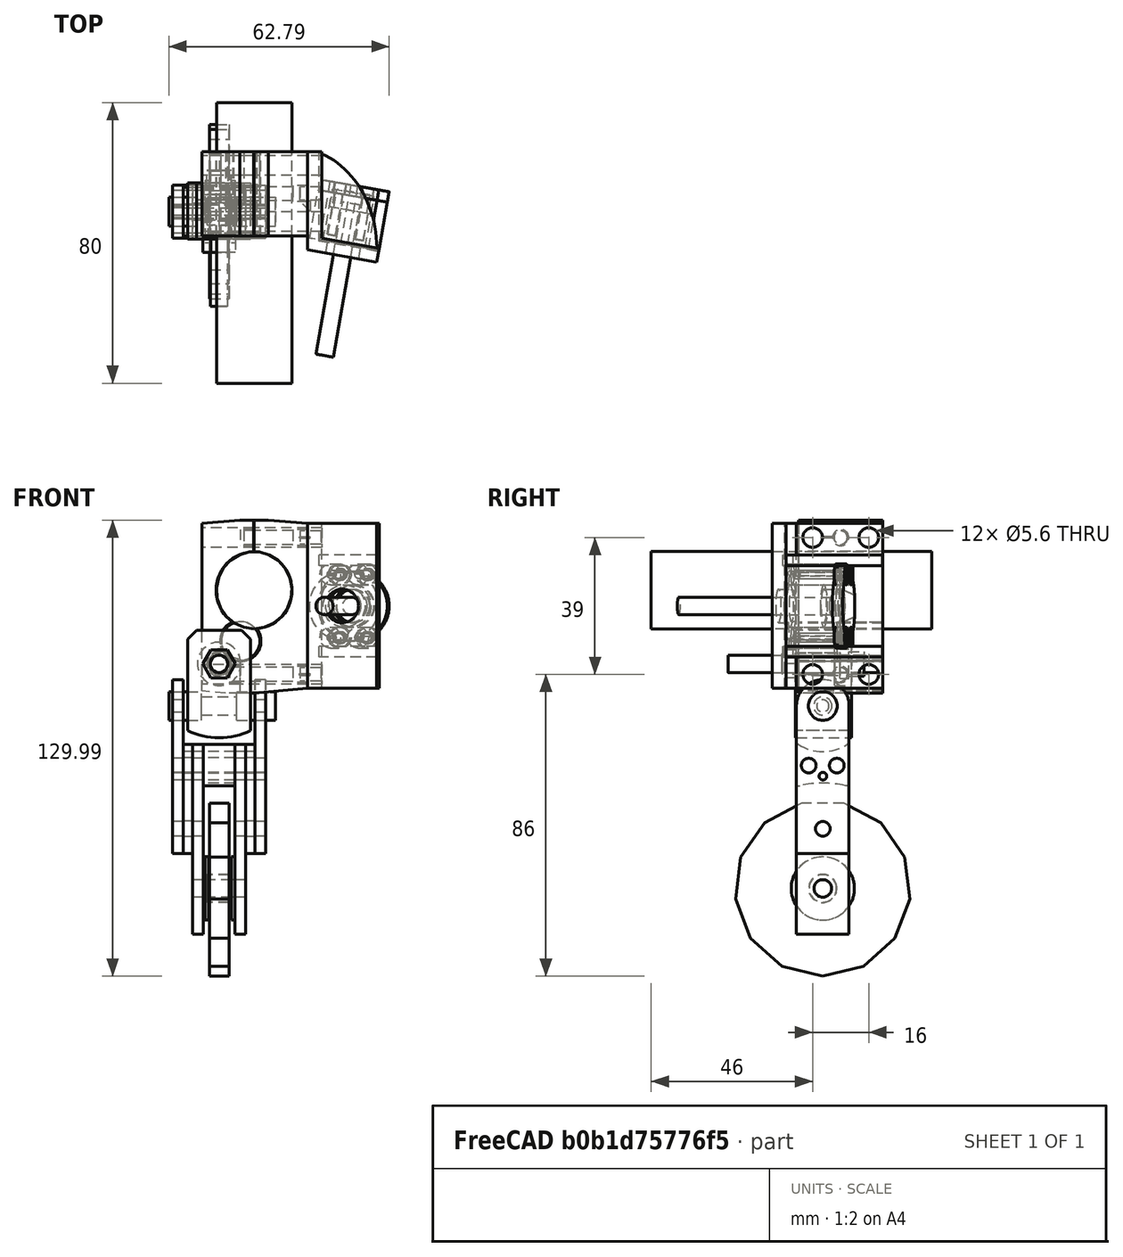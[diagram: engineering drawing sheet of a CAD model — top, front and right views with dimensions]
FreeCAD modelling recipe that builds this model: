
FCSTD DOCUMENT  (FreeCAD 0.18R4 (GitTag))
Label: ~ketten_spanner_118
License: All rights reserved
LicenseURL: http://en.wikipedia.org/wiki/All_rights_reserved
objects: Part::Cylinder×56, Part::Cut×43, Sketcher::SketchObject×37, PartDesign::Body×37, App::DocumentObjectGroup×35, PartDesign::Pad×29, App::Part×13, PartDesign::Revolution×5, Mesh::Feature×3
note: 241 computed .brp shape members not serialized (recipe doc carries the construction recipe); baked Part::Feature solids carry a one-line shape summary decoded from their .brp

FEATURE [Sketcher::SketchObject] Sketch001
  MapMode = 5
  Placement = pos=(0,0,0) rot=(1,0,0;1.5708rad)
  Support = -> [XZ_Plane002]
  sketch-geometry (6):
    g0: Ellipse CenterX=10 CenterY=21 CenterZ=0 NormalX=0 NormalY=0 NormalZ=1 MajorRadius=11 MinorRadius=10.75 AngleXU=-1.5708
    g1: LineSegment [constr] StartX=10 StartY=10 StartZ=0 EndX=10 EndY=32 EndZ=0
    g2: LineSegment [constr] StartX=20.75 StartY=21 StartZ=0 EndX=-0.75 EndY=21 EndZ=0
    g3: GeomPoint X=10 Y=18.6682 Z=0
    g4: GeomPoint X=10 Y=23.3318 Z=0
    g5: LineSegment [constr] StartX=-7.94652 StartY=18.6682 StartZ=0 EndX=23.4716 EndY=18.6682 EndZ=0
  constraints (8):
    c: InternalAlignment(g1-g4 -> g0) x4
    c: Vertical(g1)
    c: DistanceY(g1,g1) = 22
    c: DistanceX(g2,g2) = 21.5
    c: DistanceX(g-1,g1) = 10
    c: DistanceY(g-1,g1) = 10
    c: Horizontal(g5)
    c: PointOnObject(g3,g5)
FEATURE [PartDesign::Pad] Pad
  Length = 80
  Length2 = 100
  Placement = pos=(0,0,0) rot=(1,0,0;1.5708rad)
  Profile = -> Sketch001
  Type = 0
FEATURE [PartDesign::Body] Body001  label="schwinge_P"
  Group = -> [Sketch001,Pad]
  Origin = -> Origin002
  Placement = pos=(0,14,0) rot=(0,0,1;0rad)
  Tip = -> Pad
FEATURE [Sketcher::SketchObject] Sketch002
  MapMode = 5
  Placement = pos=(0,0,0) rot=(1,0,0;1.5708rad)
  Support = -> [XZ_Plane004]
  sketch-geometry (14):
    g0: ArcOfCircle CenterX=6.11771 CenterY=6.51111 CenterZ=0 NormalX=0 NormalY=0 NormalZ=1 AngleXU=0 Radius=5.5 StartAngle=4.88029 EndAngle=10.3041
    g1: LineSegment [constr] StartX=-14.7828 StartY=10 StartZ=0 EndX=10 EndY=10 EndZ=0
    g2: LineSegment [constr] StartX=7.54122 StartY=11.8237 StartZ=0 EndX=-1.04375 EndY=-20.2158 EndZ=0
    g3: LineSegment StartX=2.6104 StartY=2.27451 StartZ=0 EndX=7.03683 EndY=1.08845 EndZ=0
    g4: LineSegment [constr] StartX=2.6104 StartY=2.27451 StartZ=0 EndX=5.328 EndY=12.4167 EndZ=0
    g5: LineSegment [constr] StartX=5.328 StartY=12.4167 StartZ=0 EndX=7.54122 EndY=11.8237 EndZ=0
    g6: LineSegment [constr] StartX=10 StartY=34.9897 StartZ=0 EndX=10 EndY=-5.77115 EndZ=0
    g7: LineSegment [constr] StartX=10 StartY=21 StartZ=0 EndX=-1.04375 EndY=-20.2158 EndZ=0
    g8: LineSegment [constr] StartX=10 StartY=10 StartZ=0 EndX=10 EndY=32 EndZ=0
    g9: LineSegment [constr] StartX=-6.34284 StartY=21 StartZ=0 EndX=23.447 EndY=21 EndZ=0
    g10: LineSegment [constr] StartX=8.31393 StartY=14.7075 StartZ=0 EndX=12.847 EndY=31.6252 EndZ=0
    g11: Circle [constr] CenterX=10 CenterY=21 CenterZ=0 NormalX=0 NormalY=0 NormalZ=1 AngleXU=0 Radius=11
    g12: LineSegment [constr] StartX=4.48461 StartY=9.26913 StartZ=0 EndX=10.6338 EndY=32.2182 EndZ=0
    g13: LineSegment [constr] StartX=10.6338 StartY=32.2182 StartZ=0 EndX=12.847 EndY=31.6252 EndZ=0
  constraints (38):
    c: Horizontal(g1)
    c: DistanceY(g-1,g1) = 10
    c: PointOnObject(g0,g2)
    c: Coincident(g3,g0)
    c: Coincident(g3,g0)
    c: Radius(g0) = 5.5
    c: PointOnObject(g2,g0)
    c: Perpendicular(g2,g3)
    c: Coincident(g4,g0)
    c: Parallel(g4,g2)
    c: Coincident(g5,g2)
    c: Coincident(g5,g4)
    c: Perpendicular(g5,g4)
    c: Vertical(g6)
    c: DistanceX(g-1,g6) = 10
    c: PointOnObject(g7,g6)
    c: Angle(g6,g7) = -0.261799
    c: PointOnObject(g2,g7)
    c: Coincident(g2,g7)
    c: Vertical(g8)
    c: PointOnObject(g8,g1)
    c: DistanceY(g8,g8) = 22
    c: PointOnObject(g8,g6)
    c: Horizontal(g9)
    c: Symmetric(g1,g8,g9)
    c: PointOnObject(g7,g9)
    c: PointOnObject(g10,g7)
    c: Parallel(g10,g2)
    c: Coincident(g11,g7)
    c: Radius(g11) = 11
    c: PointOnObject(g10,g11)
    c: Distance(g10,g0) = 26
    c: PointOnObject(g12,g4)
    c: Parallel(g12,g4)
    c: Coincident(g13,g12)
    c: Coincident(g13,g10)
    c: Perpendicular(g12,g13)
    c: Distance(g12,g0) = 31
FEATURE [PartDesign::Pad] Pad001
  Length = 13
  Length2 = 100
  Placement = pos=(0,0,0) rot=(1,0,0;1.5708rad)
  Profile = -> Sketch002
  Type = 0
FEATURE [PartDesign::Body] Body  label="Bremsspanner_P"
  Group = -> [Sketch002,Pad001]
  Origin = -> Origin003
  Tip = -> Pad001
FEATURE [PartDesign::Body] Body002  label="klemme_P"
  Origin = -> Origin005
FEATURE [PartDesign::Body] Body003  label="platte_P"
  Origin = -> Origin006
FEATURE [Sketcher::SketchObject] Sketch
  MapMode = 5
  Placement = pos=(0,0,0) rot=(1,0,0;1.5708rad)
  sketch-geometry (22):
    g0: LineSegment [constr] StartX=9.89353 StartY=-3.73516 StartZ=0 EndX=9.89353 EndY=38.9018 EndZ=0
    g1: ArcOfCircle CenterX=6.01 CenterY=6.5 CenterZ=0 NormalX=0 NormalY=0 NormalZ=1 AngleXU=0 Radius=5.8 StartAngle=1.95124 EndAngle=4.69231
    g2: LineSegment [constr] StartX=5.89353 StartY=0.701169 StartZ=0 EndX=6.01 EndY=6.5 EndZ=0
    g3: LineSegment [constr] StartX=6.01 StartY=6.5 StartZ=0 EndX=3.85628 EndY=11.8853 EndZ=0
    g4: LineSegment [constr] StartX=9.89353 StartY=20.9935 StartZ=0 EndX=-1.15445 EndY=-20.2381 EndZ=0
    g5: LineSegment [constr] StartX=9.89353 StartY=20.9935 StartZ=0 EndX=9.89353 EndY=-21.8961 EndZ=0
    g6: ArcOfEllipse CenterX=9.89353 CenterY=20.9935 CenterZ=0 NormalX=0 NormalY=0 NormalZ=1 MajorRadius=11 MinorRadius=10.7674 AngleXU=1.5708 StartAngle=0 EndAngle=2.54637
    g7: LineSegment [constr] StartX=9.89353 StartY=31.9935 StartZ=0 EndX=9.89353 EndY=9.99354 EndZ=0
    g8: GeomPoint X=9.89353 Y=23.2435 Z=0
    g9: GeomPoint X=9.89353 Y=18.7435 Z=0
    g10: LineSegment [constr] StartX=8.83076 StartY=17.0272 StartZ=0 EndX=12.6435 EndY=31.2567 EndZ=0
    g11: LineSegment [constr] StartX=9.89353 StartY=31.9935 StartZ=0 EndX=12.6435 EndY=31.2567 EndZ=0
    g12: LineSegment StartX=5.89353 StartY=0.701169 StartZ=0 EndX=5.89353 EndY=-8.29883 EndZ=0
    g13: LineSegment StartX=5.89353 StartY=-8.29883 StartZ=0 EndX=1.89353 EndY=-8.29883 EndZ=0
    g14: LineSegment StartX=1.89353 StartY=-8.29883 StartZ=0 EndX=-4.8739 EndY=-7.70676 EndZ=0
    g15: LineSegment StartX=-4.8739 StartY=-7.70676 StartZ=0 EndX=-4.8739 EndY=40.0515 EndZ=0
    g16: LineSegment StartX=-4.8739 StartY=40.0515 StartZ=0 EndX=5.89353 EndY=40.9935 EndZ=0
    g17: LineSegment StartX=5.89353 StartY=40.9935 StartZ=0 EndX=9.89353 EndY=40.9935 EndZ=0
    g18: LineSegment StartX=9.89353 StartY=40.9935 StartZ=0 EndX=9.89353 EndY=31.9935 EndZ=0
    g19: LineSegment [constr] StartX=1.89353 StartY=-8.29883 StartZ=0 EndX=-7.766 EndY=-8.29883 EndZ=0
    g20: LineSegment [constr] StartX=5.89353 StartY=40.9935 StartZ=0 EndX=-7.21475 EndY=40.9935 EndZ=0
    g21: LineSegment [constr] StartX=9.89353 StartY=20.9935 StartZ=0 EndX=-0.873896 EndY=20.9935 EndZ=0
  constraints (56):
    c: Vertical(g0)
    c: Radius(g1) = 5.8
    c: Coincident(g2,g1)
    c: Coincident(g2,g1)
    c: Coincident(g3,g1)
    c: Vertical(g5)
    c: Angle(g5,g4) = -0.261799
    c: PointOnObject(g1,g4)
    c: InternalAlignment(g7,g6)
    c: InternalAlignment(g8,g6)
    c: InternalAlignment(g9,g6)
    c: Vertical(g7)
    c: Coincident(g4,g5)
    c: Coincident(g4,g6)
    c: PointOnObject(g10,g4)
    c: Coincident(g11,g7)
    c: Coincident(g11,g10)
    c: Parallel(g10,g4)
    c: Perpendicular(g10,g11)
    c: Coincident(g12,g13)
    c: Coincident(g13,g14)
    c: Coincident(g14,g15)
    c: Vertical(g15)
    c: Coincident(g15,g16)
    c: Coincident(g16,g17)
    c: Coincident(g17,g18)
    c: Vertical(g18)
    c: Coincident(g12,g1)
    c: Coincident(g6,g18)
    c: Vertical(g12)
    c: Horizontal(g13)
    c: Coincident(g19,g13)
    c: Horizontal(g19)
    c: Angle(g14,g19) = 0.0872665
    c: Horizontal(g17)
    c: DistanceY(g6,g17) = 9
    c: Coincident(g20,g16)
    c: Horizontal(g20)
    c: Angle(g20,g16) = 0.0872665
    c: DistanceX(g13,g12) = 4
    c: DistanceX(g16,g17) = 4
    c: DistanceX(g-1,g1) = 6.01
    c: PointOnObject(g17,g0)
    c: DistanceY(g-1,g1) = 6.5
    c: Coincident(g3,g1)
    c: Coincident(g1,g6)
    c: PointOnObject(g0,g5)
    c: DistanceY(g7,g6) = 22
    c: DistanceY(g12,g1) = 9
    c: Distance(g1,g10) = 25.63
    c: DistanceX(g12,g5) = 4
    c: Coincident(g21,g6)
    c: Horizontal(g21)
    c: PointOnObject(g21,g6)
    c: DistanceX(g14,g21) = 4
    c: DistanceY(g9,g8) = 4.5
FEATURE [PartDesign::Pad] Pad002
  Length = 24
  Length2 = 100
  Placement = pos=(0,0,0) rot=(1,0,0;1.5708rad)
  Profile = -> Sketch
  Type = 0
FEATURE [Sketcher::SketchObject] Sketch003
  MapMode = 5
  Placement = pos=(0,0,0) rot=(1,0,0;1.5708rad)
  sketch-geometry (25):
    g0: LineSegment [constr] StartX=10 StartY=-2.49556 StartZ=0 EndX=10 EndY=51.298 EndZ=0
    g1: ArcOfCircle CenterX=6.11647 CenterY=6.5 CenterZ=0 NormalX=0 NormalY=0 NormalZ=1 AngleXU=0 Radius=5.8 StartAngle=4.69231 EndAngle=6.93504
    g2: LineSegment [constr] StartX=10.7272 StartY=10.0187 StartZ=0 EndX=6.11647 EndY=6.5 EndZ=0
    g3: LineSegment [constr] StartX=6.11647 StartY=6.5 StartZ=0 EndX=6 EndY=0.701169 EndZ=0
    g4: LineSegment [constr] StartX=10 StartY=20.9935 StartZ=0 EndX=-1.05913 EndY=-20.2797 EndZ=0
    g5: LineSegment [constr] StartX=10 StartY=20.9935 StartZ=0 EndX=10 EndY=-21.8961 EndZ=0
    g6: ArcOfEllipse CenterX=10 CenterY=20.9935 CenterZ=0 NormalX=0 NormalY=0 NormalZ=1 MajorRadius=11 MinorRadius=10.7674 AngleXU=1.5708 StartAngle=3.20918 EndAngle=6.28319
    g7: LineSegment [constr] StartX=10 StartY=31.9935 StartZ=0 EndX=10 EndY=9.99354 EndZ=0
    g8: GeomPoint X=10 Y=23.2435 Z=0
    g9: GeomPoint X=10 Y=18.7435 Z=0
    g10: LineSegment [constr] StartX=8.44517 StartY=15.1908 StartZ=0 EndX=12.75 EndY=31.2567 EndZ=0
    g11: LineSegment [constr] StartX=10 StartY=31.9935 StartZ=0 EndX=12.75 EndY=31.2567 EndZ=0
    g12: LineSegment [constr] StartX=2.90768 StartY=-8 StartZ=0 EndX=-7.766 EndY=-8 EndZ=0
    g13: LineSegment [constr] StartX=6 StartY=40.954 StartZ=0 EndX=-7.21475 EndY=40.954 EndZ=0
    g14: LineSegment StartX=10 StartY=31.9935 StartZ=0 EndX=10 EndY=40.9935 EndZ=0
    g15: LineSegment StartX=10 StartY=40.9935 StartZ=0 EndX=14 EndY=40.9935 EndZ=0
    g16: LineSegment StartX=14 StartY=40.9935 StartZ=0 EndX=25.2674 EndY=40.0078 EndZ=0
    g17: LineSegment StartX=25.2674 StartY=40.0078 StartZ=0 EndX=25.2674 EndY=-6.9631 EndZ=0
    g18: LineSegment StartX=25.2674 StartY=-6.9631 StartZ=0 EndX=10 EndY=-8.29883 EndZ=0
    g19: LineSegment StartX=10 StartY=-8.29883 StartZ=0 EndX=6 EndY=-8.29883 EndZ=0
    g20: LineSegment StartX=6 StartY=-8.29883 StartZ=0 EndX=6 EndY=0.701169 EndZ=0
    g21: LineSegment [constr] StartX=10 StartY=-8.29883 StartZ=0 EndX=29.3759 EndY=-8.29883 EndZ=0
    g22: LineSegment [constr] StartX=14 StartY=40.9935 StartZ=0 EndX=28.0792 EndY=40.9935 EndZ=0
    g23: LineSegment [constr] StartX=6 StartY=0.701169 StartZ=0 EndX=16.0779 EndY=0.701169 EndZ=0
    g24: LineSegment [constr] StartX=10 StartY=20.9935 StartZ=0 EndX=20.7674 EndY=20.9935 EndZ=0
  constraints (60):
    c: Vertical(g0)
    c: Radius(g1) = 5.8
    c: Coincident(g2,g1)
    c: Coincident(g2,g1)
    c: Coincident(g3,g1)
    c: Coincident(g3,g1)
    c: Vertical(g5)
    c: Angle(g5,g4) = -0.261799
    c: PointOnObject(g1,g4)
    c: InternalAlignment(g7,g6)
    c: InternalAlignment(g8,g6)
    c: InternalAlignment(g9,g6)
    c: Vertical(g7)
    c: DistanceX(g-1,g6) = 10
    c: Coincident(g4,g5)
    c: Coincident(g4,g6)
    c: PointOnObject(g10,g4)
    c: PointOnObject(g0,g7)
    c: Coincident(g11,g7)
    c: Coincident(g11,g10)
    c: Parallel(g10,g4)
    c: Perpendicular(g10,g11)
    c: Distance(g10,g1) = 25.63
    c: Horizontal(g12)
    c: Horizontal(g13)
    c: Coincident(g6,g1)
    c: Vertical(g14)
    c: Coincident(g14,g15)
    c: Horizontal(g15)
    c: Coincident(g15,g16)
    c: Coincident(g16,g17)
    c: Vertical(g17)
    c: Coincident(g18,g19)
    c: Horizontal(g19)
    c: Coincident(g19,g20)
    c: Vertical(g20)
    c: Coincident(g20,g1)
    c: Coincident(g14,g6)
    c: Horizontal(g21)
    c: DistanceX(g14,g15) = 4
    c: Coincident(g22,g15)
    c: Horizontal(g22)
    c: Angle(g16,g22) = 0.0872665
    c: DistanceY(g7,g7) = 22
    c: Coincident(g23,g1)
    c: Horizontal(g23)
    c: DistanceY(g6,g14) = 9
    c: DistanceY(g-1,g1) = 6.5
    c: PointOnObject(g14,g0)
    c: DistanceX(g19,g5) = 4
    c: Coincident(g24,g6)
    c: Horizontal(g24)
    c: PointOnObject(g24,g6)
    c: DistanceX(g24,g17) = 4.5
    c: Coincident(g18,g17)
    c: PointOnObject(g18,g5)
    c: Coincident(g21,g18)
    c: Angle(g21,g18) = 0.0872665
    c: DistanceY(g21,g23) = 9
    c: DistanceY(g9,g8) = 4.5
FEATURE [PartDesign::Pad] Pad003
  Length = 24
  Length2 = 100
  Placement = pos=(0,0,0) rot=(1,0,0;1.5708rad)
  Profile = -> Sketch003
  Type = 0
FEATURE [Part::Cylinder] Cylinder  label="O1"
  Angle = 360
  AttacherType = Attacher::AttachEngine3D
  Height = 60
  Placement = pos=(41,-20,36) rot=(0,-1,0;1.5708rad)
  Radius = 2.8
FEATURE [Part::Cylinder] Cylinder001  label="O2"
  Angle = 360
  AttacherType = Attacher::AttachEngine3D
  Height = 60
  Placement = pos=(41,-4,36) rot=(0,-1,0;1.5708rad)
  Radius = 2.8
FEATURE [Part::Cylinder] Cylinder002  label="U001"
  Angle = 360
  AttacherType = Attacher::AttachEngine3D
  Height = 60
  Placement = pos=(41,-4,-3) rot=(0,-1,0;1.5708rad)
  Radius = 2.8
FEATURE [Part::Cylinder] Cylinder003  label="U002"
  Angle = 360
  AttacherType = Attacher::AttachEngine3D
  Height = 60
  Placement = pos=(41,-20,-3) rot=(0,-1,0;1.5708rad)
  Radius = 2.8
FEATURE [Part::Cylinder] Cylinder004  label="O003"
  Angle = 360
  AttacherType = Attacher::AttachEngine3D
  Height = 60
  Placement = pos=(41,-4,36) rot=(0,-1,0;1.5708rad)
  Radius = 2.8
FEATURE [Part::Cylinder] Cylinder005  label="U003"
  Angle = 360
  AttacherType = Attacher::AttachEngine3D
  Height = 60
  Placement = pos=(41,-20,-3) rot=(0,-1,0;1.5708rad)
  Radius = 2.8
FEATURE [Part::Cylinder] Cylinder006  label="U004"
  Angle = 360
  AttacherType = Attacher::AttachEngine3D
  Height = 60
  Placement = pos=(41,-4,-3) rot=(0,-1,0;1.5708rad)
  Radius = 2.8
FEATURE [Part::Cylinder] Cylinder007  label="O004"
  Angle = 360
  AttacherType = Attacher::AttachEngine3D
  Height = 60
  Placement = pos=(41,-20,36) rot=(0,-1,0;1.5708rad)
  Radius = 2.8
FEATURE [App::Part] Part002  label="Bremsspanner"
  Group = -> [Body]
  Origin = -> Origin007
  Placement = pos=(0,-5.5,0) rot=(0,0,1;0rad)
FEATURE [App::Part] Part005  label="Holm"
  Group = -> [Body001]
  Origin = -> Origin010
  Placement = pos=(0,2,0) rot=(0,0,1;0rad)
FEATURE [App::Part] Part  label="Basis"
  Group = -> [Part002,Part005]
  Origin = -> Origin
FEATURE [Part::Cylinder] Cylinder010  label="PassI_Pl-Kl0"
  Angle = 360
  AttacherType = Attacher::AttachEngine3D
  Height = 35
  Placement = pos=(41,-12,36) rot=(0,-1,0;1.5708rad)
  Radius = 2.3
FEATURE [Part::Cylinder] Cylinder011  label="PassI_Pl-Kl1"
  Angle = 360
  AttacherType = Attacher::AttachEngine3D
  Height = 39
  Placement = pos=(41,-12,-3) rot=(0,-1,0;1.5708rad)
  Radius = 2.3
FEATURE [Part::Cylinder] Cylinder012  label="PassO_Pl-Kl0"
  Angle = 360
  AttacherType = Attacher::AttachEngine3D
  Height = 14
  Placement = pos=(21,-12,36) rot=(0,-1,0;1.5708rad)
  Radius = 2
FEATURE [Part::Cylinder] Cylinder013  label="PassO_Pl-Kl1"
  Angle = 360
  AttacherType = Attacher::AttachEngine3D
  Height = 18
  Placement = pos=(21,-12,-3) rot=(0,-1,0;1.5708rad)
  Radius = 2
FEATURE [Part::Cylinder] Cylinder014  label="PassI_Kl-Wi0"
  Angle = 360
  AttacherType = Attacher::AttachEngine3D
  Height = 20
  Placement = pos=(41,-12,-3) rot=(0,-1,0;1.5708rad)
  Radius = 2.3
FEATURE [Part::Cylinder] Cylinder015  label="PassI_Kl-Wi1"
  Angle = 360
  AttacherType = Attacher::AttachEngine3D
  Height = 20
  Placement = pos=(41,-12,36) rot=(0,-1,0;1.5708rad)
  Radius = 2.3
FEATURE [Sketcher::SketchObject] Sketch005
  MapMode = 5
  Placement = pos=(0,0,0) rot=(1,0,0;1.5708rad)
  Support = -> [XZ_Plane016]
  sketch-geometry (12):
    g0: ArcOfEllipse CenterX=6.11474 CenterY=6.5 CenterZ=0 NormalX=0 NormalY=0 NormalZ=1 MajorRadius=5.5 MinorRadius=5.49977 AngleXU=1.309 StartAngle=0.640981 EndAngle=5.62359
    g1: LineSegment [constr] StartX=7.53824 StartY=11.8126 StartZ=0 EndX=4.69123 EndY=1.18741 EndZ=0
    g2: GeomPoint X=6.12768 Y=6.5483 Z=0
    g3: GeomPoint X=6.1018 Y=6.4517 Z=0
    g4: LineSegment [constr] StartX=10 StartY=27.7324 StartZ=0 EndX=10 EndY=-9.55565 EndZ=0
    g5: LineSegment [constr] StartX=10 StartY=21 StartZ=0 EndX=2.09145 EndY=-8.5151 EndZ=0
    g6: ArcOfEllipse CenterX=6.11474 CenterY=6.5 CenterZ=0 NormalX=0 NormalY=0 NormalZ=1 MajorRadius=5.8 MinorRadius=5.79978 AngleXU=-1.8326 StartAngle=3.79757 EndAngle=8.76184
    g7: LineSegment [constr] StartX=4.61359 StartY=0.89763 StartZ=0 EndX=7.61589 EndY=12.1024 EndZ=0
    g8: GeomPoint X=6.1018 Y=6.4517 Z=0
    g9: GeomPoint X=6.12768 Y=6.5483 Z=0
    g10: LineSegment StartX=10.4951 StartY=9.82594 StartZ=0 EndX=10.7457 EndY=9.99187 EndZ=0
    g11: LineSegment StartX=3.88738 StartY=11.8552 StartZ=0 EndX=4.07899 EndY=11.6093 EndZ=0
  constraints (24):
    c: InternalAlignment(g1,g0)
    c: InternalAlignment(g2,g0)
    c: InternalAlignment(g3,g0)
    c: Vertical(g4)
    c: DistanceX(g-1,g4) = 10
    c: PointOnObject(g5,g4)
    c: Angle(g5,g4) = 0.261799
    c: DistanceY(g-1,g5) = 21
    c: PointOnObject(g0,g5)
    c: PointOnObject(g1,g5)
    c: DistanceY(g-1,g0) = 6.5
    c: Distance(g1,g1) = 11
    c: Distance(g2,g3) = 0.1
    c: InternalAlignment(g7,g6)
    c: InternalAlignment(g8,g6)
    c: InternalAlignment(g9,g6)
    c: Distance(g9,g8) = 0.1
    c: PointOnObject(g7,g1)
    c: Distance(g7,g7) = 11.6
    c: Coincident(g6,g0)
    c: Coincident(g0,g11)
    c: Coincident(g11,g6)
    c: Coincident(g10,g0)
    c: Coincident(g10,g6)
FEATURE [PartDesign::Pad] Pad005
  Length = 24
  Length2 = 100
  Placement = pos=(0,0,0) rot=(1,0,0;1.5708rad)
  Profile = -> Sketch005
  Type = 0
FEATURE [PartDesign::Body] Body005  label="Pressung"
  Group = -> [Sketch005,Pad005]
  Origin = -> Origin015
  Tip = -> Pad005
FEATURE [App::Part] Part008  label="Einlage"
  Group = -> [Body005]
  Origin = -> Origin014
FEATURE [Part::Cut] Cut
  Base = -> Pad002
  Tool = -> Cylinder
FEATURE [Part::Cut] Cut010
  Base = -> Cut
  Tool = -> Cylinder002
FEATURE [Part::Cut] Cut011
  Base = -> Cut010
  Tool = -> Cylinder003
FEATURE [Part::Cut] Cut012
  Base = -> Cut011
  Tool = -> Cylinder001
FEATURE [Part::Cut] Cut013
  Base = -> Cut012
  Tool = -> Cylinder010
FEATURE [Part::Cut] Cut014
  Base = -> Cut013
  Tool = -> Cylinder011
FEATURE [App::Part] Part003  label="platte"
  Group = -> [Body003,Cylinder001,Cylinder003,Cylinder002,Cylinder,Sketch,Pad002,Cylinder010,Cylinder011,Cut,Cut010,Cut011,Cut012,Cut013,Cut014]
  Origin = -> Origin008
FEATURE [Part::Cut] Cut015
  Base = -> Pad003
  Tool = -> Cylinder007
FEATURE [Part::Cut] Cut016
  Base = -> Cut015
  Tool = -> Cylinder006
FEATURE [Part::Cut] Cut017
  Base = -> Cut016
  Tool = -> Cylinder005
FEATURE [Part::Cut] Cut018
  Base = -> Cut017
  Tool = -> Cylinder004
FEATURE [Part::Cut] Cut019
  Base = -> Cut018
  Tool = -> Cylinder015
FEATURE [Part::Cut] Cut020
  Base = -> Cut019
  Tool = -> Cylinder014
FEATURE [App::Part] Part004  label="klemme"
  Group = -> [Body002,Cylinder004,Cylinder005,Cylinder006,Cylinder007,Sketch003,Pad003,Cylinder012,Cylinder013,Cylinder014,Cylinder015,Cut015,Cut016,Cut017,Cut018,Cut019,Cut020]
  Origin = -> Origin009
FEATURE [App::DocumentObjectGroup] Gruppe  label="platte001"
FEATURE [App::DocumentObjectGroup] Gruppe001  label="~"
FEATURE [App::DocumentObjectGroup] Group001  label="klemme001"
  Group = -> [Gruppe001]
FEATURE [Sketcher::SketchObject] Sketch006
  MapMode = 5
  Support = -> [XY_Plane016]
  sketch-geometry (10):
    g0: LineSegment StartX=29.25 StartY=0 StartZ=0 EndX=25.25 EndY=0 EndZ=0
    g1: LineSegment StartX=25.25 StartY=0 StartZ=0 EndX=25.25 EndY=-28 EndZ=0
    g2: LineSegment StartX=25.25 StartY=-28 StartZ=0 EndX=44.9462 EndY=-31.473 EndZ=0
    g3: LineSegment StartX=44.9462 StartY=-31.473 StartZ=0 EndX=45.6407 EndY=-27.5337 EndZ=0
    g4: LineSegment StartX=45.6407 StartY=-27.5337 StartZ=0 EndX=29.25 EndY=-24.6436 EndZ=0
    g5: LineSegment StartX=29.25 StartY=-24.6436 StartZ=0 EndX=29.25 EndY=0 EndZ=0
    g6: LineSegment [constr] StartX=29.25 StartY=-24.6436 StartZ=0 EndX=39.6032 EndY=-24.6436 EndZ=0
    g7: LineSegment [constr] StartX=20 StartY=17.7351 StartZ=0 EndX=20 EndY=-46.6544 EndZ=0
    g8: LineSegment [constr] StartX=46 StartY=18.5698 StartZ=0 EndX=46 EndY=-45.1043 EndZ=0
    g9: LineSegment [constr] StartX=39.4477 StartY=-5.06867 StartZ=0 EndX=33.7885 EndY=-37.1635 EndZ=0
  constraints (26):
    c: Coincident(g0,g1)
    c: Vertical(g1)
    c: Coincident(g1,g2)
    c: Coincident(g2,g3)
    c: Coincident(g3,g4)
    c: Coincident(g4,g5)
    c: Coincident(g5,g0)
    c: Horizontal(g0)
    c: Vertical(g5)
    c: Perpendicular(g3,g2)
    c: Parallel(g2,g4)
    c: DistanceX(g-1,g0) = 25.25
    c: DistanceY(g0,g-1) = 0
    c: DistanceY(g1,g0) = 28
    c: DistanceX(g0,g0) = 4
    c: Distance(g2,g3) = 4
    c: Coincident(g6,g4)
    c: Horizontal(g6)
    c: Angle(g4,g6) = 0.174533
    c: Distance(g1,g2) = 20
    c: Vertical(g7)
    c: DistanceX(g-1,g7) = 20
    c: Vertical(g8)
    c: DistanceX(g7,g8) = 26
    c: Perpendicular(g2,g9)
    c: Distance(g3,g9) = 10
FEATURE [PartDesign::Pad] Pad006
  Length = 47
  Length2 = 100
  Profile = -> Sketch006
  Type = 0
FEATURE [PartDesign::Body] Body006  label="winkel_p"
  Group = -> [Sketch006,Pad006]
  Origin = -> Origin016
  Placement = pos=(0,0,-7) rot=(0,0,1;0rad)
  Tip = -> Pad006
FEATURE [Part::Cylinder] Cylinder016  label="U005"
  Angle = 360
  AttacherType = Attacher::AttachEngine3D
  Height = 60
  Placement = pos=(41,-4,-3) rot=(0,-1,0;1.5708rad)
  Radius = 2.8
FEATURE [Part::Cylinder] Cylinder017  label="U006"
  Angle = 360
  AttacherType = Attacher::AttachEngine3D
  Height = 60
  Placement = pos=(41,-20,-3) rot=(0,-1,0;1.5708rad)
  Radius = 2.8
FEATURE [Part::Cylinder] Cylinder019  label="PassO_Pl-Kl002"
  Angle = 360
  AttacherType = Attacher::AttachEngine3D
  Height = 6
  Placement = pos=(29,-12,36) rot=(0,-1,0;1.5708rad)
  Radius = 1.9
FEATURE [Part::Cylinder] Cylinder020  label="PassO_Pl-Kl003"
  Angle = 360
  AttacherType = Attacher::AttachEngine3D
  Height = 6
  Placement = pos=(29,-12,-3) rot=(0,-1,0;1.5708rad)
  Radius = 1.9
FEATURE [Part::Cylinder] Cylinder021  label="O005"
  Angle = 360
  AttacherType = Attacher::AttachEngine3D
  Height = 60
  Placement = pos=(41,-20,36) rot=(0,-1,0;1.5708rad)
  Radius = 2.8
FEATURE [Part::Cylinder] Cylinder022  label="O006"
  Angle = 360
  AttacherType = Attacher::AttachEngine3D
  Height = 60
  Placement = pos=(41,-4,36) rot=(0,-1,0;1.5708rad)
  Radius = 2.8
FEATURE [Sketcher::SketchObject] Sketch007
  MapMode = 5
  Support = -> [XY_Plane018]
  sketch-geometry (8):
    g0: ArcOfEllipse CenterX=21.5 CenterY=-28 CenterZ=0 NormalX=0 NormalY=0 NormalZ=1 MajorRadius=29 MinorRadius=23.5 AngleXU=-1.5708 StartAngle=1.55669 EndAngle=2.83913
    g1: LineSegment [constr] StartX=21.5 StartY=-57 StartZ=0 EndX=21.5 EndY=1 EndZ=0
    g2: LineSegment [constr] StartX=45 StartY=-28 StartZ=0 EndX=-2 EndY=-28 EndZ=0
    g3: GeomPoint X=21.5 Y=-44.9926 Z=0
    g4: GeomPoint X=21.5 Y=-11.0074 Z=0
    g5: LineSegment StartX=44.9977 StartY=-28.409 StartZ=0 EndX=28.5 EndY=-25.5 EndZ=0
    g6: LineSegment StartX=28.5 StartY=-25.5 StartZ=0 EndX=28.5 EndY=-0.316434 EndZ=0
    g7: LineSegment [constr] StartX=28.5 StartY=-25.5 StartZ=0 EndX=39.983 EndY=-25.5 EndZ=0
  constraints (15):
    c: InternalAlignment(g1-g4 -> g0) x4
    c: Vertical(g1)
    c: DistanceY(g0,g-1) = 28
    c: DistanceX(g-1,g0) = 21.5
    c: DistanceY(g2,g1) = 29
    c: DistanceX(g0,g2) = 23.5
    c: Coincident(g5,g0)
    c: Coincident(g5,g6)
    c: Coincident(g6,g0)
    c: Vertical(g6)
    c: Coincident(g7,g5)
    c: Horizontal(g7)
    c: Angle(g5,g7) = 0.174533
    c: DistanceY(g5,g-1) = 25.5
    c: DistanceX(g-1,g0) = 28.5
FEATURE [PartDesign::Pad] Pad007
  Length = 3
  Length2 = 100
  Profile = -> Sketch007
  Type = 0
FEATURE [PartDesign::Body] Body008  label="steg_U"
  Group = -> [Sketch007,Pad007]
  Origin = -> Origin018
  Placement = pos=(0,0,2) rot=(0,0,1;0rad)
  Tip = -> Pad007
FEATURE [Sketcher::SketchObject] Sketch008
  MapMode = 5
  Support = -> [XY_Plane019]
  sketch-geometry (8):
    g0: ArcOfEllipse CenterX=21.5 CenterY=-28 CenterZ=0 NormalX=0 NormalY=0 NormalZ=1 MajorRadius=29 MinorRadius=23.5 AngleXU=-1.5708 StartAngle=1.55669 EndAngle=2.83913
    g1: LineSegment [constr] StartX=21.5 StartY=-57 StartZ=0 EndX=21.5 EndY=1 EndZ=0
    g2: LineSegment [constr] StartX=45 StartY=-28 StartZ=0 EndX=-2 EndY=-28 EndZ=0
    g3: GeomPoint X=21.5 Y=-44.9926 Z=0
    g4: GeomPoint X=21.5 Y=-11.0074 Z=0
    g5: LineSegment StartX=44.9977 StartY=-28.409 StartZ=0 EndX=28.5 EndY=-25.5 EndZ=0
    g6: LineSegment StartX=28.5 StartY=-25.5 StartZ=0 EndX=28.5 EndY=-0.316434 EndZ=0
    g7: LineSegment [constr] StartX=28.5 StartY=-25.5 StartZ=0 EndX=39.983 EndY=-25.5 EndZ=0
  constraints (15):
    c: InternalAlignment(g1-g4 -> g0) x4
    c: Vertical(g1)
    c: DistanceY(g0,g-1) = 28
    c: DistanceX(g-1,g0) = 21.5
    c: DistanceY(g2,g1) = 29
    c: DistanceX(g0,g2) = 23.5
    c: Coincident(g5,g0)
    c: Coincident(g5,g6)
    c: Coincident(g6,g0)
    c: Vertical(g6)
    c: Coincident(g7,g5)
    c: Horizontal(g7)
    c: Angle(g5,g7) = 0.174533
    c: DistanceX(g-1,g0) = 28.5
    c: DistanceY(g5,g-1) = 25.5
FEATURE [PartDesign::Pad] Pad008
  Length = 3
  Length2 = 100
  Profile = -> Sketch008
  Type = 0
FEATURE [PartDesign::Body] Body009  label="steg_O"
  Group = -> [Sketch008,Pad008]
  Origin = -> Origin019
  Placement = pos=(0,0,28) rot=(0,0,1;0rad)
  Tip = -> Pad008
FEATURE [Part::Cylinder] Cylinder023  label="lager_O"
  Angle = 360
  AttacherType = Attacher::AttachEngine3D
  Height = 14
  Placement = pos=(35.6525,-26.4333,16.5) rot=(-0.992433,0.086826,-0.086826;1.57839rad)
  Radius = 10
FEATURE [Part::Cylinder] Cylinder024  label="bohrung_durch_0"
  Angle = 360
  AttacherType = Attacher::AttachEngine3D
  Height = 9
  Placement = pos=(33.9135,-36.2781,15.5) rot=(-0.992433,0.086826,-0.086826;1.57839rad)
  Radius = 4.75
FEATURE [Part::Cylinder] Cylinder025  label="bohrung_lager"
  Angle = 360
  AttacherType = Attacher::AttachEngine3D
  Height = 18
  Placement = pos=(35.6525,-26.4333,16.5) rot=(-0.992433,0.086826,-0.086826;1.57839rad)
  Radius = 6.05
FEATURE [Part::Cylinder] Cylinder026  label="bohrung_durch_1"
  Angle = 360
  AttacherType = Attacher::AttachEngine3D
  Height = 16
  Placement = pos=(33.9135,-36.2781,16.5) rot=(-0.992433,0.086826,-0.086826;1.57839rad)
  Radius = 4.75
FEATURE [Part::Cut] Cut021
  Base = -> Body006
  Tool = -> Cylinder026
FEATURE [Part::Cut] Cut022
  Base = -> Cylinder023
  Tool = -> Cylinder024
FEATURE [Part::Cut] Cut023
  Base = -> Cut022
  Tool = -> Cylinder025
FEATURE [Part::Cut] Cut024
  Base = -> Cut021
  Tool = -> Cylinder021
FEATURE [Part::Cut] Cut025
  Base = -> Cut024
  Tool = -> Cylinder022
FEATURE [Part::Cut] Cut026
  Base = -> Cut025
  Tool = -> Cylinder016
FEATURE [Part::Cut] Cut027
  Base = -> Cut026
  Tool = -> Cylinder017
FEATURE [App::DocumentObjectGroup] Group004  label="winkel_F"
  Group = -> [Cut027]
FEATURE [Part::Cylinder] Cylinder027  label="befestigung_0"
  Angle = 360
  AttacherType = Attacher::AttachEngine3D
  Height = 14
  Placement = pos=(31.7108,-25.7354,7.5) rot=(-0.992433,0.086826,-0.086826;1.57839rad)
  Radius = 3
FEATURE [App::DocumentObjectGroup] Group005  label="befestigung"
FEATURE [Part::Cylinder] Cylinder028  label="befestigung_1"
  Angle = 360
  AttacherType = Attacher::AttachEngine3D
  Height = 14
  Placement = pos=(31.7108,-25.7355,25.5) rot=(-0.992433,0.086826,-0.086826;1.57839rad)
  Radius = 3
FEATURE [Sketcher::SketchObject] Sketch009
  MapMode = 5
  Support = -> [XY_Plane020]
  sketch-geometry (3):
    g0: LineSegment StartX=23 StartY=-14 StartZ=0 EndX=26 EndY=-14 EndZ=0
    g1: LineSegment StartX=26 StartY=-14 StartZ=0 EndX=26 EndY=-17 EndZ=0
    g2: LineSegment StartX=26 StartY=-17 StartZ=0 EndX=23 EndY=-14 EndZ=0
  constraints (9):
    c: Horizontal(g0)
    c: Coincident(g2,g0)
    c: DistanceX(g0,g0) = 3
    c: Angle(g1,g2) = 0.785398
    c: Coincident(g1,g0)
    c: DistanceX(g-1,g0) = 26
    c: DistanceY(g0,g-1) = 14
    c: Vertical(g1)
    c: Coincident(g1,g2)
FEATURE [PartDesign::Pad] Pad009
  Length = 0.4
  Length2 = 100
  Profile = -> Sketch009
  Type = 0
FEATURE [PartDesign::Body] Body010  label="stütze_0"
  Group = -> [Sketch009,Pad009]
  Origin = -> Origin020
  Placement = pos=(-0.1,0,-3.2) rot=(0,0,1;0rad)
  Tip = -> Pad009
FEATURE [Sketcher::SketchObject] Sketch010
  MapMode = 5
  Support = -> [XY_Plane021]
  sketch-geometry (3):
    g0: LineSegment StartX=23 StartY=-14 StartZ=0 EndX=26 EndY=-14 EndZ=0
    g1: LineSegment StartX=26 StartY=-14 StartZ=0 EndX=26 EndY=-17 EndZ=0
    g2: LineSegment StartX=26 StartY=-17 StartZ=0 EndX=23 EndY=-14 EndZ=0
  constraints (9):
    c: Vertical(g1)
    c: Horizontal(g0)
    c: Coincident(g2,g0)
    c: DistanceX(g0,g0) = 3
    c: Angle(g1,g2) = 0.785398
    c: DistanceX(g-1,g0) = 26
    c: DistanceY(g0,g-1) = 14
    c: Coincident(g2,g1)
    c: Coincident(g1,g0)
FEATURE [PartDesign::Pad] Pad010
  Length = 0.4
  Length2 = 100
  Profile = -> Sketch010
  Type = 0
FEATURE [PartDesign::Body] Body011  label="stütze_001"
  Group = -> [Sketch010,Pad010]
  Origin = -> Origin021
  Placement = pos=(-0.1,0,35.8) rot=(0,0,1;0rad)
  Tip = -> Pad010
FEATURE [App::DocumentObjectGroup] Group003  label="hilfen"
  Group = -> [Body010,Body011]
FEATURE [Part::Cylinder] Cylinder029  label="befestigung_2"
  Angle = 360
  AttacherType = Attacher::AttachEngine3D
  Height = 14
  Placement = pos=(39.5892,-27.1246,25.5) rot=(-0.992433,0.086826,-0.086826;1.57839rad)
  Radius = 3
FEATURE [Part::Cylinder] Cylinder030  label="befestigung_3"
  Angle = 360
  AttacherType = Attacher::AttachEngine3D
  Height = 14
  Placement = pos=(39.5892,-27.1246,7.5) rot=(-0.992433,0.086826,-0.086826;1.57839rad)
  Radius = 3
FEATURE [App::DocumentObjectGroup] Gruppe002  label="~001"
FEATURE [App::DocumentObjectGroup] Group006  label="halter001"
  Group = -> [Gruppe002]
FEATURE [Part::Cylinder] Cylinder031  label="bef_bohrung_0"
  Angle = 360
  AttacherType = Attacher::AttachEngine3D
  Height = 14
  Placement = pos=(32.0552,-23.766,7.50001) rot=(-0.992433,0.086826,-0.086826;1.57839rad)
  Radius = 1.25
FEATURE [Part::Cylinder] Cylinder032  label="bef_bohrung_1"
  Angle = 360
  AttacherType = Attacher::AttachEngine3D
  Height = 14
  Placement = pos=(32.0581,-23.7658,25.5) rot=(-0.992433,0.086826,-0.086826;1.57839rad)
  Radius = 1.25
FEATURE [Part::Cylinder] Cylinder033  label="bef_bohrung_2"
  Angle = 360
  AttacherType = Attacher::AttachEngine3D
  Height = 14
  Placement = pos=(39.9365,-25.155,25.5) rot=(-0.992433,0.086826,-0.086826;1.57839rad)
  Radius = 1.25
FEATURE [Part::Cylinder] Cylinder034  label="bef_bohrung_3"
  Angle = 360
  AttacherType = Attacher::AttachEngine3D
  Height = 14
  Placement = pos=(39.9365,-25.1549,7.50001) rot=(-0.992433,0.086826,-0.086826;1.57839rad)
  Radius = 1.25
FEATURE [Part::Cylinder] Cylinder035  label="bef_bohrung_004"
  Angle = 360
  AttacherType = Attacher::AttachEngine3D
  Height = 14
  Placement = pos=(32.0581,-23.7658,25.5) rot=(-0.992433,0.086826,-0.086826;1.57839rad)
  Radius = 1.25
FEATURE [Part::Cylinder] Cylinder036  label="bef_bohrung_005"
  Angle = 360
  AttacherType = Attacher::AttachEngine3D
  Height = 14
  Placement = pos=(39.9365,-25.1549,7.50001) rot=(-0.992433,0.086826,-0.086826;1.57839rad)
  Radius = 1.25
FEATURE [Part::Cylinder] Cylinder037  label="bef_bohrung_006"
  Angle = 360
  AttacherType = Attacher::AttachEngine3D
  Height = 14
  Placement = pos=(39.9365,-25.155,25.5) rot=(-0.992433,0.086826,-0.086826;1.57839rad)
  Radius = 1.25
FEATURE [Part::Cylinder] Cylinder038  label="bef_bohrung_007"
  Angle = 360
  AttacherType = Attacher::AttachEngine3D
  Height = 14
  Placement = pos=(32.0552,-23.766,7.50001) rot=(-0.992433,0.086826,-0.086826;1.57839rad)
  Radius = 1.25
FEATURE [Part::Cut] Cut028
  Base = -> Cut023
  Tool = -> Cylinder031
FEATURE [Part::Cut] Cut029
  Base = -> Cut028
  Tool = -> Cylinder032
FEATURE [Part::Cut] Cut030
  Base = -> Cut029
  Tool = -> Cylinder033
FEATURE [Part::Cut] Cut031
  Base = -> Cut030
  Tool = -> Cylinder034
FEATURE [App::DocumentObjectGroup] Gruppe003  label="bef_bohrung_A"
  Group = -> [Cut031]
FEATURE [Part::Cut] Cut032
  Base = -> Cylinder027
  Tool = -> Cylinder038
FEATURE [Part::Cut] Cut033
  Base = -> Cylinder028
  Tool = -> Cylinder035
FEATURE [Part::Cut] Cut034
  Base = -> Cylinder029
  Tool = -> Cylinder037
FEATURE [Part::Cut] Cut035
  Base = -> Cylinder030
  Tool = -> Cylinder036
FEATURE [App::DocumentObjectGroup] Gruppe004  label="bef_bohrung_I"
  Group = -> [Cut032,Cut033,Cut034,Cut035]
FEATURE [App::DocumentObjectGroup] Group002  label="lager_F"
  Group = -> [Group005,Gruppe003,Gruppe004]
FEATURE [App::Part] Part006  label="winkel"
  Group = -> [Body006,Cylinder016,Cylinder017,Cylinder019,Cylinder020,Cylinder021,Cylinder022,Body008,Body009,Cylinder023,Group002,Group003,Cylinder024,Cylinder025,Cylinder026,Group004,Cut021,Cut022,Cut023,Cut024,Cut025,Cut026,Cut027,Cylinder027,Group005,Cylinder028,Body010,Body011,Cylinder029,Cylinder030,Cylinder031,Gruppe003,Cylinder032,Cylinder033,Cylinder034,Cylinder035,Cylinder036,Cylinder037,Cylinder038,+9 more]
  Origin = -> Origin011
FEATURE [App::Part] Part001  label="halter"
  Group = -> [Part003,Part004,Part006,Part008]
  Origin = -> Origin004
FEATURE [App::DocumentObjectGroup] Group007  label="welle-ref_F"
FEATURE [Part::Cylinder] Cylinder039  label="bohrung_durch_002"
  Angle = 360
  AttacherType = Attacher::AttachEngine3D
  Height = 44
  Placement = pos=(30.0586,-58.1408,16.4999) rot=(-0.992433,0.086826,-0.086826;1.57839rad)
  Radius = 2.5
FEATURE [Part::Cylinder] Cylinder040  label="befestigung_004"
  Angle = 360
  AttacherType = Attacher::AttachEngine3D
  Height = 3
  Placement = pos=(42.0203,-13.3373,25.5001) rot=(-0.992433,0.086826,-0.086826;1.57839rad)
  Radius = 3
FEATURE [Part::Cylinder] Cylinder041  label="befestigung_005"
  Angle = 360
  AttacherType = Attacher::AttachEngine3D
  Height = 3
  Placement = pos=(34.1418,-11.9481,25.5001) rot=(-0.992433,0.086826,-0.086826;1.57839rad)
  Radius = 3
FEATURE [Part::Cylinder] Cylinder042  label="befestigung_006"
  Angle = 360
  AttacherType = Attacher::AttachEngine3D
  Height = 3
  Placement = pos=(34.1418,-11.9481,7.50006) rot=(-0.992433,0.086826,-0.086826;1.57839rad)
  Radius = 3
FEATURE [Part::Cylinder] Cylinder043  label="bef_bohrung_008"
  Angle = 360
  AttacherType = Attacher::AttachEngine3D
  Height = 18
  Placement = pos=(32.0581,-23.7658,25.5) rot=(-0.992433,0.086826,-0.086826;1.57839rad)
  Radius = 1.75
FEATURE [Part::Cylinder] Cylinder044  label="bef_bohrung_009"
  Angle = 360
  AttacherType = Attacher::AttachEngine3D
  Height = 18
  Placement = pos=(39.9365,-25.1549,7.50001) rot=(-0.992433,0.086826,-0.086826;1.57839rad)
  Radius = 1.75
FEATURE [Part::Cylinder] Cylinder045  label="befestigung_007"
  Angle = 360
  AttacherType = Attacher::AttachEngine3D
  Height = 3
  Placement = pos=(42.0203,-13.3372,7.50005) rot=(-0.992433,0.086826,-0.086826;1.57839rad)
  Radius = 3
FEATURE [Part::Cut] Cut037
  Base = -> Cylinder045
  Tool = -> Cylinder044
FEATURE [Part::Cylinder] Cylinder046  label="bef_bohrung_010"
  Angle = 360
  AttacherType = Attacher::AttachEngine3D
  Height = 19
  Placement = pos=(39.9365,-25.155,25.5) rot=(-0.992433,0.086826,-0.086826;1.57839rad)
  Radius = 1.75
FEATURE [Part::Cut] Cut036
  Base = -> Cylinder040
  Tool = -> Cylinder046
FEATURE [Part::Cylinder] Cylinder047  label="bef_bohrung_011"
  Angle = 360
  AttacherType = Attacher::AttachEngine3D
  Height = 18
  Placement = pos=(32.0552,-23.766,7.50001) rot=(-0.992433,0.086826,-0.086826;1.57839rad)
  Radius = 1.75
FEATURE [Part::Cut] Cut038
  Base = -> Cylinder042
  Tool = -> Cylinder047
FEATURE [Part::Cut] Cut039
  Base = -> Cylinder041
  Tool = -> Cylinder043
FEATURE [Part::Cylinder] Cylinder051  label="bef_bohrung_012"
  Angle = 360
  AttacherType = Attacher::AttachEngine3D
  Height = 18
  Placement = pos=(32.0581,-23.7658,25.5) rot=(-0.992433,0.086826,-0.086826;1.57839rad)
  Radius = 1.75
FEATURE [Part::Cylinder] Cylinder053  label="bef_bohrung_014"
  Angle = 360
  AttacherType = Attacher::AttachEngine3D
  Height = 18
  Placement = pos=(39.9365,-25.155,25.5) rot=(-0.992433,0.086826,-0.086826;1.57839rad)
  Radius = 1.75
FEATURE [Part::Cylinder] Cylinder054  label="bef_bohrung_015"
  Angle = 360
  AttacherType = Attacher::AttachEngine3D
  Height = 18
  Placement = pos=(32.0552,-23.766,7.50001) rot=(-0.992433,0.086826,-0.086826;1.57839rad)
  Radius = 1.75
FEATURE [Part::Cylinder] Cylinder055  label="lager_O002"
  Angle = 360
  AttacherType = Attacher::AttachEngine3D
  Height = 3
  Placement = pos=(38.0836,-12.646,16.5) rot=(-0.992433,0.086826,-0.086826;1.57839rad)
  Radius = 10
FEATURE [Part::Cylinder] Cylinder059  label="bef_bohrung_017"
  Angle = 360
  AttacherType = Attacher::AttachEngine3D
  Height = 18
  Placement = pos=(39.9365,-25.1549,7.50001) rot=(-0.992433,0.086826,-0.086826;1.57839rad)
  Radius = 1.75
FEATURE [Part::Cylinder] Cylinder062  label="lager_O003"
  Angle = 360
  AttacherType = Attacher::AttachEngine3D
  Height = 5.1
  Placement = pos=(37.389,-16.5852,16.5) rot=(-0.992433,0.086826,-0.086826;1.57839rad)
  Radius = 6
FEATURE [Part::Cylinder] Cylinder063  label="bohrung_durch_005"
  Angle = 360
  AttacherType = Attacher::AttachEngine3D
  Height = 18
  Placement = pos=(35.1464,-29.2859,16.5) rot=(-0.992433,0.086826,-0.086826;1.57839rad)
  Radius = 4.8
FEATURE [App::DocumentObjectGroup] Gruppe009  label="~002"
FEATURE [App::DocumentObjectGroup] Gruppe008  label="lagerdeckel001"
  Group = -> [Gruppe009]
FEATURE [Part::Cut] Cut053
  Base = -> Cylinder055
  Tool = -> Cylinder059
FEATURE [Part::Cut] Cut054
  Base = -> Cut053
  Tool = -> Cylinder054
FEATURE [Part::Cut] Cut055
  Base = -> Cut054
  Tool = -> Cylinder053
FEATURE [Sketcher::SketchObject] Sketch011
  MapMode = 5
  Support = -> [XY_Plane027]
  sketch-geometry (10):
    g0: LineSegment StartX=29.25 StartY=0 StartZ=0 EndX=25.25 EndY=0 EndZ=0
    g1: LineSegment StartX=25.25 StartY=0 StartZ=0 EndX=25.25 EndY=-28 EndZ=0
    g2: LineSegment StartX=25.25 StartY=-28 StartZ=0 EndX=44.9462 EndY=-31.473 EndZ=0
    g3: LineSegment StartX=44.9462 StartY=-31.473 StartZ=0 EndX=45.6407 EndY=-27.5337 EndZ=0
    g4: LineSegment StartX=45.6407 StartY=-27.5337 StartZ=0 EndX=29.25 EndY=-24.6436 EndZ=0
    g5: LineSegment StartX=29.25 StartY=-24.6436 StartZ=0 EndX=29.25 EndY=0 EndZ=0
    g6: LineSegment [constr] StartX=29.25 StartY=-24.6436 StartZ=0 EndX=39.6032 EndY=-24.6436 EndZ=0
    g7: LineSegment [constr] StartX=20 StartY=17.7351 StartZ=0 EndX=20 EndY=-46.6544 EndZ=0
    g8: LineSegment [constr] StartX=46 StartY=18.5698 StartZ=0 EndX=46 EndY=-45.1043 EndZ=0
    g9: LineSegment [constr] StartX=39.4477 StartY=-5.06867 StartZ=0 EndX=33.7885 EndY=-37.1635 EndZ=0
  constraints (26):
    c: Coincident(g0,g1)
    c: Vertical(g1)
    c: Coincident(g1,g2)
    c: Coincident(g2,g3)
    c: Coincident(g3,g4)
    c: Coincident(g4,g5)
    c: Coincident(g5,g0)
    c: Horizontal(g0)
    c: Vertical(g5)
    c: Perpendicular(g3,g2)
    c: Parallel(g2,g4)
    c: DistanceX(g-1,g0) = 25.25
    c: DistanceY(g0,g-1) = 0
    c: DistanceY(g1,g0) = 28
    c: DistanceX(g0,g0) = 4
    c: Distance(g2,g3) = 4
    c: Coincident(g6,g4)
    c: Horizontal(g6)
    c: Angle(g4,g6) = 0.174533
    c: Distance(g1,g2) = 20
    c: Vertical(g7)
    c: DistanceX(g-1,g7) = 20
    c: Vertical(g8)
    c: DistanceX(g7,g8) = 26
    c: Perpendicular(g2,g9)
    c: Distance(g3,g9) = 10
FEATURE [PartDesign::Pad] Pad011
  Length = 47
  Length2 = 100
  Profile = -> Sketch011
  Type = 0
FEATURE [PartDesign::Body] Body013  label="winkel_p001"
  Group = -> [Sketch011,Pad011]
  Origin = -> Origin027
  Placement = pos=(0,0,-7) rot=(0,0,1;0rad)
  Tip = -> Pad011
FEATURE [Sketcher::SketchObject] Sketch012
  MapMode = 5
  Support = -> [XY_Plane028]
  sketch-geometry (8):
    g0: ArcOfEllipse CenterX=21.5 CenterY=-28 CenterZ=0 NormalX=0 NormalY=0 NormalZ=1 MajorRadius=29 MinorRadius=23.5 AngleXU=-1.5708 StartAngle=1.55669 EndAngle=2.83913
    g1: LineSegment [constr] StartX=21.5 StartY=-57 StartZ=0 EndX=21.5 EndY=1 EndZ=0
    g2: LineSegment [constr] StartX=45 StartY=-28 StartZ=0 EndX=-2 EndY=-28 EndZ=0
    g3: GeomPoint X=21.5 Y=-44.9926 Z=0
    g4: GeomPoint X=21.5 Y=-11.0074 Z=0
    g5: LineSegment StartX=44.9977 StartY=-28.409 StartZ=0 EndX=28.5 EndY=-25.5 EndZ=0
    g6: LineSegment StartX=28.5 StartY=-25.5 StartZ=0 EndX=28.5 EndY=-0.316434 EndZ=0
    g7: LineSegment [constr] StartX=28.5 StartY=-25.5 StartZ=0 EndX=39.983 EndY=-25.5 EndZ=0
  constraints (15):
    c: InternalAlignment(g1-g4 -> g0) x4
    c: Vertical(g1)
    c: DistanceY(g0,g-1) = 28
    c: DistanceX(g-1,g0) = 21.5
    c: DistanceY(g2,g1) = 29
    c: DistanceX(g0,g2) = 23.5
    c: Coincident(g5,g0)
    c: Coincident(g5,g6)
    c: Coincident(g6,g0)
    c: Vertical(g6)
    c: Coincident(g7,g5)
    c: Horizontal(g7)
    c: Angle(g5,g7) = 0.174533
    c: DistanceY(g5,g-1) = 25.5
    c: DistanceX(g-1,g0) = 28.5
FEATURE [PartDesign::Pad] Pad012
  Length = 3
  Length2 = 100
  Profile = -> Sketch012
  Type = 0
FEATURE [PartDesign::Body] Body014  label="steg_U001"
  Group = -> [Sketch012,Pad012]
  Origin = -> Origin028
  Placement = pos=(0,0,2) rot=(0,0,1;0rad)
  Tip = -> Pad012
FEATURE [Sketcher::SketchObject] Sketch013
  MapMode = 5
  Support = -> [XY_Plane029]
  sketch-geometry (8):
    g0: ArcOfEllipse CenterX=21.5 CenterY=-28 CenterZ=0 NormalX=0 NormalY=0 NormalZ=1 MajorRadius=29 MinorRadius=23.5 AngleXU=-1.5708 StartAngle=1.55669 EndAngle=2.83913
    g1: LineSegment [constr] StartX=21.5 StartY=-57 StartZ=0 EndX=21.5 EndY=1 EndZ=0
    g2: LineSegment [constr] StartX=45 StartY=-28 StartZ=0 EndX=-2 EndY=-28 EndZ=0
    g3: GeomPoint X=21.5 Y=-44.9926 Z=0
    g4: GeomPoint X=21.5 Y=-11.0074 Z=0
    g5: LineSegment StartX=44.9977 StartY=-28.409 StartZ=0 EndX=28.5 EndY=-25.5 EndZ=0
    g6: LineSegment StartX=28.5 StartY=-25.5 StartZ=0 EndX=28.5 EndY=-0.316434 EndZ=0
    g7: LineSegment [constr] StartX=28.5 StartY=-25.5 StartZ=0 EndX=39.983 EndY=-25.5 EndZ=0
  constraints (15):
    c: InternalAlignment(g1-g4 -> g0) x4
    c: Vertical(g1)
    c: DistanceY(g0,g-1) = 28
    c: DistanceX(g-1,g0) = 21.5
    c: DistanceY(g2,g1) = 29
    c: DistanceX(g0,g2) = 23.5
    c: Coincident(g5,g0)
    c: Coincident(g5,g6)
    c: Coincident(g6,g0)
    c: Vertical(g6)
    c: Coincident(g7,g5)
    c: Horizontal(g7)
    c: Angle(g5,g7) = 0.174533
    c: DistanceX(g-1,g0) = 28.5
    c: DistanceY(g5,g-1) = 25.5
FEATURE [PartDesign::Pad] Pad013
  Length = 3
  Length2 = 100
  Profile = -> Sketch013
  Type = 0
FEATURE [PartDesign::Body] Body015  label="steg_O001"
  Group = -> [Sketch013,Pad013]
  Origin = -> Origin029
  Placement = pos=(0,0,28) rot=(0,0,1;0rad)
  Tip = -> Pad013
FEATURE [Part::Cut] Cut058
  Base = -> Cut038
  Tool = -> Body014
FEATURE [Part::Cut] Cut059
  Base = -> Cut039
  Tool = -> Body015
FEATURE [App::DocumentObjectGroup] Gruppe005  label="befestigungen"
  Group = -> [Cut037,Cut036,Cut058,Cut059]
FEATURE [Part::Cut] Cut056
  Base = -> Cut055
  Tool = -> Cylinder051
FEATURE [Part::Cut] Cut057
  Base = -> Cut056
  Tool = -> Body013
FEATURE [Part::Cylinder] Cylinder064  label="bohrung_durch_006"
  Angle = 360
  AttacherType = Attacher::AttachEngine3D
  Height = 18
  Placement = pos=(35.1464,-29.2859,16.5) rot=(-0.992433,0.086826,-0.086826;1.57839rad)
  Radius = 4.8
FEATURE [Part::Cut] Cut060
  Base = -> Cylinder062
  Placement = pos=(0,-0.2,0) rot=(0,0,1;0rad)
  Tool = -> Cylinder063
FEATURE [App::DocumentObjectGroup] Gruppe007  label="haltering"
  Group = -> [Cut060]
FEATURE [Part::Cut] Cut061
  Base = -> Cut057
  Tool = -> Cylinder064
FEATURE [App::DocumentObjectGroup] Gruppe006  label="abdeckung"
  Group = -> [Cut061]
FEATURE [App::DocumentObjectGroup] Group008  label="lagerdeckel"
  Group = -> [Gruppe005,Gruppe006,Gruppe007]
FEATURE [App::Part] Part012  label="lagerdeckel_P"
  Group = -> [Group008,Cylinder046,Cylinder040,Cut036,Cylinder045,Cylinder044,Cut037,Cylinder047,Cylinder042,Cut038,Cylinder041,Cylinder043,Cut039,Gruppe005,Cylinder051,Cylinder053,Cylinder054,Gruppe006,Cylinder055,Cylinder059,Gruppe007,Cylinder062,Cylinder063,Cut053,Cut054,Cut055,Cut056,Body013,Body014,Body015,Cut057,Cut058,Cut059,Cylinder064,Cut060,Cut061]
  Origin = -> Origin026
FEATURE [Sketcher::SketchObject] CopySketch016
  Placement = pos=(0,0,0) rot=(0.57735,0.57735,0.57735;2.0944rad)
  sketch-geometry (6):
    g0: LineSegment StartX=-2.49921 StartY=-3.5 StartZ=0 EndX=-2.49921 EndY=-2.5 EndZ=0
    g1: LineSegment StartX=-2.49921 StartY=-2.5 StartZ=0 EndX=-9.29921 EndY=-2.5 EndZ=0
    g2: LineSegment StartX=-9.29921 StartY=-2.5 StartZ=0 EndX=-9.29921 EndY=-4.2 EndZ=0
    g3: LineSegment StartX=-9.29921 StartY=-4.2 StartZ=0 EndX=-6.79921 EndY=-4.2 EndZ=0
    g4: LineSegment StartX=-6.79921 StartY=-4.2 StartZ=0 EndX=-6.79921 EndY=-3.5 EndZ=0
    g5: LineSegment StartX=-6.79921 StartY=-3.5 StartZ=0 EndX=-2.49921 EndY=-3.5 EndZ=0
  constraints (17):
    c: Vertical(g0)
    c: Coincident(g0,g1)
    c: Horizontal(g1)
    c: Coincident(g1,g2)
    c: Vertical(g2)
    c: Coincident(g2,g3)
    c: Coincident(g3,g4)
    c: Coincident(g4,g5)
    c: Coincident(g5,g0)
    c: Horizontal(g5)
    c: Vertical(g4)
    c: Horizontal(g3)
    c: DistanceX(g2,g3) = 2.5
    c: DistanceX(g2,g0) = 6.8
    c: DistanceY(g0,g-1) = 3.5
    c: DistanceY(g0,g-1) = 2.5
    c: DistanceY(g3,g-1) = 4.2
FEATURE [PartDesign::Revolution] Revolution002
  Angle = 360
  Axis = (3e-16,1,-2e-16)
  Base = (0,0,0)
  Placement = pos=(0,0,0) rot=(0.57735,0.57735,0.57735;2.0944rad)
  Profile = -> CopySketch016
  ReferenceAxis = -> CopySketch016 [H_Axis]
  Reversed = true
FEATURE [PartDesign::Body] Body025  label="abstand-ring002"
  Group = -> [Revolution002]
  Origin = -> Origin043
  Placement = pos=(0,-2.9,-1e-15) rot=(0,0,1;0rad)
  Tip = -> Revolution002
FEATURE [Sketcher::SketchObject] Sketch018
  MapMode = 5
  Placement = pos=(0,0,0) rot=(1,0,0;1.5708rad)
  Support = -> [XZ_Plane044]
  sketch-geometry (2):
    g0: Circle CenterX=0 CenterY=0 CenterZ=0 NormalX=0 NormalY=0 NormalZ=1 AngleXU=0 Radius=2.5
    g1: Circle CenterX=0 CenterY=0 CenterZ=0 NormalX=0 NormalY=0 NormalZ=1 AngleXU=0 Radius=3.2
  constraints (4):
    c: Coincident(g0,g-1)
    c: Radius(g0) = 2.5
    c: Coincident(g1,g0)
    c: Radius(g1) = 3.2
FEATURE [Sketcher::SketchObject] Sketch019
  MapMode = 5
  Placement = pos=(0,0,0) rot=(1,0,0;1.5708rad)
  Support = -> [XZ_Plane045]
  sketch-geometry (9):
    g0: Circle CenterX=0 CenterY=0 CenterZ=0 NormalX=0 NormalY=0 NormalZ=1 AngleXU=0 Radius=2.5
    g1: Circle [constr] CenterX=0 CenterY=0 CenterZ=0 NormalX=0 NormalY=0 NormalZ=1 AngleXU=0 Radius=4.6188
    g2: LineSegment StartX=4.6188 StartY=0 StartZ=0 EndX=2.3094 EndY=4 EndZ=0
    g3: LineSegment StartX=2.3094 StartY=4 StartZ=0 EndX=-2.3094 EndY=4 EndZ=0
    g4: LineSegment StartX=-2.3094 StartY=4 StartZ=0 EndX=-4.6188 EndY=-1.89577e-11 EndZ=0
    g5: LineSegment StartX=-4.6188 StartY=-1.89579e-11 StartZ=0 EndX=-2.3094 EndY=-4 EndZ=0
    g6: LineSegment StartX=-2.3094 StartY=-4 StartZ=0 EndX=2.3094 EndY=-4 EndZ=0
    g7: LineSegment StartX=2.3094 StartY=-4 StartZ=0 EndX=4.6188 EndY=0 EndZ=0
    g8: Circle [constr] CenterX=0 CenterY=0 CenterZ=0 NormalX=0 NormalY=0 NormalZ=1 AngleXU=0 Radius=4.6188
  constraints (20):
    c: Coincident(g0,g-1)
    c: Radius(g0) = 2.5
    c: Coincident(g1,g0)
    c: Coincident(g2,g3)
    c: Coincident(g3,g4)
    c: Coincident(g4,g5)
    c: Coincident(g5,g6)
    c: Coincident(g6,g7)
    c: Coincident(g7,g2)
    c: Equal(g2, g3-g7) x5
    c: PointOnObject(g2,g8)
    c: PointOnObject(g3,g8)
    c: PointOnObject(g4,g8)
    c: PointOnObject(g5,g8)
    c: PointOnObject(g6,g8)
    c: PointOnObject(g7,g8)
    c: Coincident(g8,g0)
    c: PointOnObject(g7,g1)
    c: PointOnObject(g2,g-1)
    c: Distance(g0,g7) = 4
FEATURE [Part::Cylinder] Cylinder067  label="bohrung_durch_009"
  Angle = 360
  AttacherType = Attacher::AttachEngine3D
  Height = 44
  Placement = pos=(-0.0414413,-44.0408,-8.42758e-05) rot=(-1,-1e-06,0;1.57079rad)
  Radius = 2.5
FEATURE [PartDesign::Pad] Pad018
  Length = 3.8
  Length2 = 100
  Placement = pos=(0,0,0) rot=(1,0,0;1.5708rad)
  Profile = -> Sketch019
  Type = 0
FEATURE [PartDesign::Body] Body027  label="spann-mutter002"
  Group = -> [Sketch019,Pad018]
  Origin = -> Origin045
  Placement = pos=(-1e-15,-24.9,0) rot=(0,0,1;0rad)
  Tip = -> Pad018
FEATURE [PartDesign::Pad] Pad019
  Length = 12.7
  Length2 = 100
  Placement = pos=(0,0,0) rot=(1,0,0;1.5708rad)
  Profile = -> Sketch018
  Type = 0
FEATURE [PartDesign::Body] Body026  label="abstand-hülse003"
  Group = -> [Sketch018,Pad019]
  Origin = -> Origin044
  Placement = pos=(0.1,-12.2,1e-15) rot=(0,0,1;0rad)
  Tip = -> Pad019
FEATURE [App::DocumentObjectGroup] Group012  label="welle_durch_F"
  Group = -> [Body025,Body026,Body027,Cylinder067]
FEATURE [App::Part] Part014  label="Welle_durch_P"
  Group = -> [Group012,Body025,Body026,Body027,Cylinder067]
  Origin = -> Origin042
  Placement = pos=(36.4481,-22.1668,16.5) rot=(0,0,1;6.10865rad)
FEATURE [App::DocumentObjectGroup] Group009  label="welle_F"
  Group = -> [Part014]
FEATURE [App::Part] Part009  label="welle-XX"
  Group = -> [Group007,Cylinder039,Group009,Part014]
  Origin = -> Origin022
FEATURE [Sketcher::SketchObject] Sketch020
  MapMode = 5
  Placement = pos=(0,0,0) rot=(1,0,0;1.5708rad)
  Support = -> [XZ_Plane048]
  sketch-geometry (9):
    g0: Circle CenterX=0 CenterY=0 CenterZ=0 NormalX=0 NormalY=0 NormalZ=1 AngleXU=0 Radius=2.5
    g1: Circle [constr] CenterX=0 CenterY=0 CenterZ=0 NormalX=0 NormalY=0 NormalZ=1 AngleXU=0 Radius=4.6188
    g2: LineSegment StartX=4.6188 StartY=0 StartZ=0 EndX=2.3094 EndY=4 EndZ=0
    g3: LineSegment StartX=2.3094 StartY=4 StartZ=0 EndX=-2.3094 EndY=4 EndZ=0
    g4: LineSegment StartX=-2.3094 StartY=4 StartZ=0 EndX=-4.6188 EndY=-1.89577e-11 EndZ=0
    g5: LineSegment StartX=-4.6188 StartY=-1.89579e-11 StartZ=0 EndX=-2.3094 EndY=-4 EndZ=0
    g6: LineSegment StartX=-2.3094 StartY=-4 StartZ=0 EndX=2.3094 EndY=-4 EndZ=0
    g7: LineSegment StartX=2.3094 StartY=-4 StartZ=0 EndX=4.6188 EndY=0 EndZ=0
    g8: Circle [constr] CenterX=0 CenterY=0 CenterZ=0 NormalX=0 NormalY=0 NormalZ=1 AngleXU=0 Radius=4.6188
  constraints (20):
    c: Coincident(g0,g-1)
    c: Radius(g0) = 2.5
    c: Coincident(g1,g0)
    c: Coincident(g2,g3)
    c: Coincident(g3,g4)
    c: Coincident(g4,g5)
    c: Coincident(g5,g6)
    c: Coincident(g6,g7)
    c: Coincident(g7,g2)
    c: Equal(g2, g3-g7) x5
    c: PointOnObject(g2,g8)
    c: PointOnObject(g3,g8)
    c: PointOnObject(g4,g8)
    c: PointOnObject(g5,g8)
    c: PointOnObject(g6,g8)
    c: PointOnObject(g7,g8)
    c: Coincident(g8,g0)
    c: PointOnObject(g7,g1)
    c: PointOnObject(g2,g-1)
    c: Distance(g0,g7) = 4
FEATURE [Part::Cylinder] Cylinder068  label="bohrung_durch_010"
  Angle = 360
  AttacherType = Attacher::AttachEngine3D
  Height = 44
  Placement = pos=(-0.0414413,-44.0408,-8.42758e-05) rot=(-1,-1e-06,0;1.57079rad)
  Radius = 2.5
FEATURE [PartDesign::Pad] Pad020
  Length = 3.8
  Length2 = 100
  Placement = pos=(0,0,0) rot=(1,0,0;1.5708rad)
  Profile = -> Sketch020
  Type = 0
FEATURE [PartDesign::Body] Body030  label="spann-mutter003"
  Group = -> [Sketch020,Pad020]
  Origin = -> Origin048
  Placement = pos=(-1e-15,-24.9,0) rot=(0,0,1;0rad)
  Tip = -> Pad020
FEATURE [Sketcher::SketchObject] CopySketch017
  Placement = pos=(0,0,0) rot=(0.57735,0.57735,0.57735;2.0944rad)
  sketch-geometry (6):
    g0: LineSegment StartX=-2.49921 StartY=-3.5 StartZ=0 EndX=-2.49921 EndY=-2.5 EndZ=0
    g1: LineSegment StartX=-2.49921 StartY=-2.5 StartZ=0 EndX=-9.29921 EndY=-2.5 EndZ=0
    g2: LineSegment StartX=-9.29921 StartY=-2.5 StartZ=0 EndX=-9.29921 EndY=-4.2 EndZ=0
    g3: LineSegment StartX=-9.29921 StartY=-4.2 StartZ=0 EndX=-6.79921 EndY=-4.2 EndZ=0
    g4: LineSegment StartX=-6.79921 StartY=-4.2 StartZ=0 EndX=-6.79921 EndY=-3.5 EndZ=0
    g5: LineSegment StartX=-6.79921 StartY=-3.5 StartZ=0 EndX=-2.49921 EndY=-3.5 EndZ=0
  constraints (17):
    c: Vertical(g0)
    c: Coincident(g0,g1)
    c: Horizontal(g1)
    c: Coincident(g1,g2)
    c: Vertical(g2)
    c: Coincident(g2,g3)
    c: Coincident(g3,g4)
    c: Coincident(g4,g5)
    c: Coincident(g5,g0)
    c: Horizontal(g5)
    c: Vertical(g4)
    c: Horizontal(g3)
    c: DistanceX(g2,g3) = 2.5
    c: DistanceX(g2,g0) = 6.8
    c: DistanceY(g0,g-1) = 3.5
    c: DistanceY(g0,g-1) = 2.5
    c: DistanceY(g3,g-1) = 4.2
FEATURE [PartDesign::Revolution] Revolution003
  Angle = 360
  Axis = (3e-16,1,-2e-16)
  Base = (0,0,0)
  Placement = pos=(0,0,0) rot=(0.57735,0.57735,0.57735;2.0944rad)
  Profile = -> CopySketch017
  ReferenceAxis = -> CopySketch017 [H_Axis]
  Reversed = true
FEATURE [PartDesign::Body] Body028  label="abstand-ring003"
  Group = -> [Revolution003]
  Origin = -> Origin049
  Placement = pos=(0,-2.9,-1e-15) rot=(0,0,1;0rad)
  Tip = -> Revolution003
FEATURE [Sketcher::SketchObject] Sketch021
  MapMode = 5
  Placement = pos=(0,0,0) rot=(1,0,0;1.5708rad)
  Support = -> [XZ_Plane050]
  sketch-geometry (2):
    g0: Circle CenterX=0 CenterY=0 CenterZ=0 NormalX=0 NormalY=0 NormalZ=1 AngleXU=0 Radius=2.5
    g1: Circle CenterX=0 CenterY=0 CenterZ=0 NormalX=0 NormalY=0 NormalZ=1 AngleXU=0 Radius=3.2
  constraints (4):
    c: Coincident(g0,g-1)
    c: Radius(g0) = 2.5
    c: Coincident(g1,g0)
    c: Radius(g1) = 3.2
FEATURE [PartDesign::Pad] Pad021
  Length = 12.7
  Length2 = 100
  Placement = pos=(0,0,0) rot=(1,0,0;1.5708rad)
  Profile = -> Sketch021
  Type = 0
FEATURE [PartDesign::Body] Body029  label="abstand-hülse004"
  Group = -> [Sketch021,Pad021]
  Origin = -> Origin047
  Placement = pos=(0.1,-12.2,1e-15) rot=(0,0,1;0rad)
  Tip = -> Pad021
FEATURE [App::DocumentObjectGroup] Group014  label="welle_const_ref_F"
  Group = -> [Body028,Body029,Body030,Cylinder068]
FEATURE [Sketcher::SketchObject] Sketch022
  MapMode = 5
  Placement = pos=(0,0,0) rot=(1,0,0;1.5708rad)
  Support = -> [XZ_Plane051]
  sketch-geometry (27):
    g0: Circle CenterX=0 CenterY=0 CenterZ=0 NormalX=0 NormalY=0 NormalZ=1 AngleXU=0 Radius=3.1
    g1: LineSegment StartX=-9 StartY=7 StartZ=0 EndX=-6.4 EndY=9.6 EndZ=0
    g2: LineSegment StartX=-6.4 StartY=9.6 StartZ=0 EndX=6.4 EndY=9.6 EndZ=0
    g3: LineSegment StartX=6.4 StartY=9.6 StartZ=0 EndX=9 EndY=7 EndZ=0
    g4: LineSegment StartX=9 StartY=7 StartZ=0 EndX=9 EndY=-19 EndZ=0
    g5: LineSegment [constr] StartX=9 StartY=-19 StartZ=0 EndX=-9 EndY=-19 EndZ=0
    g6: LineSegment StartX=-9 StartY=-19 StartZ=0 EndX=-9 EndY=7 EndZ=0
    g7: LineSegment [constr] StartX=9 StartY=7 StartZ=0 EndX=9 EndY=13.3478 EndZ=0
    g8: LineSegment [constr] StartX=-9 StartY=7 StartZ=0 EndX=-9 EndY=13.0512 EndZ=0
    g9: LineSegment [constr] StartX=0 StartY=13.2493 StartZ=0 EndX=0 EndY=-18.7834 EndZ=0
    g10: LineSegment [constr] StartX=-6.08879 StartY=3.1 StartZ=0 EndX=6.78225 EndY=3.1 EndZ=0
    g11: LineSegment [constr] StartX=-13.4313 StartY=-12 StartZ=0 EndX=18.7921 EndY=-12 EndZ=0
    g12: LineSegment [constr] StartX=-5 StartY=-9.5 StartZ=0 EndX=5 EndY=-9.5 EndZ=0
    g13: LineSegment [constr] StartX=5 StartY=-9.5 StartZ=0 EndX=5 EndY=-14.5 EndZ=0
    g14: LineSegment [constr] StartX=5 StartY=-14.5 StartZ=0 EndX=-5 EndY=-14.5 EndZ=0
    g15: LineSegment [constr] StartX=-5 StartY=-14.5 StartZ=0 EndX=-5 EndY=-9.5 EndZ=0
    g16: LineSegment [constr] StartX=5 StartY=-8 StartZ=0 EndX=9 EndY=-8 EndZ=0
    g17: LineSegment [constr] StartX=9 StartY=-8 StartZ=0 EndX=9 EndY=-16 EndZ=0
    g18: LineSegment [constr] StartX=9 StartY=-16 StartZ=0 EndX=5 EndY=-16 EndZ=0
    g19: LineSegment [constr] StartX=5 StartY=-16 StartZ=0 EndX=5 EndY=-8 EndZ=0
    g20: LineSegment [constr] StartX=-9 StartY=-8 StartZ=0 EndX=-5 EndY=-8 EndZ=0
    g21: LineSegment [constr] StartX=-5 StartY=-8 StartZ=0 EndX=-5 EndY=-16 EndZ=0
    g22: LineSegment [constr] StartX=-5 StartY=-16 StartZ=0 EndX=-9 EndY=-16 EndZ=0
    g23: LineSegment [constr] StartX=-9 StartY=-16 StartZ=0 EndX=-9 EndY=-8 EndZ=0
    g24: LineSegment [constr] StartX=-6.37193 StartY=-3.1 StartZ=0 EndX=13.5095 EndY=-3.1 EndZ=0
    g25: ArcOfCircle CenterX=2.203e-13 CenterY=0 CenterZ=0 NormalX=0 NormalY=0 NormalZ=1 AngleXU=0 Radius=21.0238 StartAngle=4.27001 EndAngle=5.15476
    g26: LineSegment [constr] StartX=-7.36072 StartY=0 StartZ=0 EndX=6.87936 EndY=0 EndZ=0
  constraints (68):
    c: Coincident(g0,g-1)
    c: Radius(g0) = 3.1
    c: Coincident(g1,g2)
    c: Horizontal(g2)
    c: Coincident(g2,g3)
    c: Coincident(g3,g4)
    c: Vertical(g4)
    c: Coincident(g4,g5)
    c: Coincident(g5,g6)
    c: Coincident(g6,g1)
    c: Vertical(g6)
    c: Coincident(g7,g3)
    c: Vertical(g7)
    c: Coincident(g8,g1)
    c: Vertical(g8)
    c: Angle(g1,g8) = 0.785398
    c: Angle(g7,g3) = 0.785398
    c: Symmetric(g4,g5,g9)
    c: DistanceX(g9,g0) = 0
    c: Horizontal(g10)
    c: Tangent(g10,g0)
    c: DistanceY(g10,g2) = 6.5
    c: Horizontal(g11)
    c: Coincident(g12,g13)
    c: Coincident(g13,g14)
    c: Coincident(g14,g15)
    c: Coincident(g15,g12)
    c: Horizontal(g12)
    c: Horizontal(g14)
    c: Vertical(g15)
    c: Symmetric(g13,g12,g11)
    c: DistanceY(g13,g12) = 5
    c: Coincident(g16,g17)
    c: Coincident(g17,g18)
    c: Coincident(g18,g19)
    c: Coincident(g19,g16)
    c: Horizontal(g16)
    c: Horizontal(g18)
    c: Vertical(g19)
    c: PointOnObject(g17,g4)
    c: PointOnObject(g12,g19)
    c: Coincident(g20,g21)
    c: Coincident(g21,g22)
    c: Coincident(g22,g23)
    c: Coincident(g23,g20)
    c: Horizontal(g20)
    c: Horizontal(g22)
    c: Vertical(g21)
    c: PointOnObject(g20,g6)
    c: PointOnObject(g12,g21)
    c: Symmetric(g17,g16,g11)
    c: Symmetric(g22,g20,g11)
    c: DistanceY(g17,g16) = 8
    c: DistanceY(g22,g20) = 8
    c: DistanceX(g20,g20) = 4
    c: DistanceX(g16,g16) = 4
    c: DistanceX(g21,g18) = 10
    c: Horizontal(g24)
    c: Tangent(g24,g0)
    c: DistanceY(g4,g18) = 3
    c: Coincident(g25,g4)
    c: Coincident(g25,g5)
    c: PointOnObject(g26,g-1)
    c: PointOnObject(g26,g-1)
    c: PointOnObject(g25,g26)
    c: Symmetric(g2,g1,g9)
    c: DistanceY(g0,g3) = 7
    c: DistanceY(g11,g-1) = 12
FEATURE [PartDesign::Pad] Pad022
  Length = 16
  Length2 = 100
  Placement = pos=(0,0,0) rot=(1,0,0;1.5708rad)
  Profile = -> Sketch022
  Type = 0
FEATURE [PartDesign::Body] Body031  label="kardan_B"
  Group = -> [Sketch022,Pad022]
  Origin = -> Origin050
  Placement = pos=(0,-8.9,0) rot=(0,0,1;0rad)
  Tip = -> Pad022
FEATURE [Part::Cylinder] Cylinder069  label="bohrung-durch-innen"
  Angle = 360
  AttacherType = Attacher::AttachEngine3D
  Height = 44
  Placement = pos=(-0.0414413,-44.0408,-8.42758e-05) rot=(-1,-1e-06,0;1.57079rad)
  Radius = 3.1
FEATURE [Sketcher::SketchObject] CopySketch018
  Placement = pos=(0,0,0) rot=(0.57735,0.57735,0.57735;2.0944rad)
  sketch-geometry (4):
    g0: LineSegment StartX=-2.49921 StartY=-6.2 StartZ=0 EndX=-2.49921 EndY=-2.5 EndZ=0
    g1: LineSegment StartX=-2.49921 StartY=-2.5 StartZ=0 EndX=-9.29921 EndY=-2.5 EndZ=0
    g2: LineSegment StartX=-9.29921 StartY=-2.5 StartZ=0 EndX=-9.29921 EndY=-6.2 EndZ=0
    g3: LineSegment StartX=-9.29921 StartY=-6.2 StartZ=0 EndX=-2.49921 EndY=-6.2 EndZ=0
  constraints (11):
    c: Vertical(g0)
    c: Coincident(g0,g1)
    c: Horizontal(g1)
    c: Coincident(g1,g2)
    c: Vertical(g2)
    c: Coincident(g2,g3)
    c: Horizontal(g3)
    c: DistanceX(g2,g0) = 6.8
    c: DistanceY(g0,g-1) = 2.5
    c: DistanceY(g3,g-1) = 6.2
    c: Coincident(g3,g0)
FEATURE [PartDesign::Revolution] Revolution004
  Angle = 360
  Axis = (0,1,0)
  Base = (0,0,0)
  Placement = pos=(0,0,0) rot=(0.57735,0.57735,0.57735;2.0944rad)
  Profile = -> CopySketch018
  ReferenceAxis = -> CopySketch018 [H_Axis]
  Reversed = true
FEATURE [PartDesign::Body] Body032  label="abstand-ring004"
  Group = -> [Revolution004]
  Origin = -> Origin051
  Placement = pos=(0,-4.4,-1e-15) rot=(0,0,1;0rad)
  Tip = -> Revolution004
FEATURE [Sketcher::SketchObject] Sketch023
  MapMode = 5
  Placement = pos=(0,0,0) rot=(1,0,0;1.5708rad)
  Support = -> [XZ_Plane053]
  sketch-geometry (9):
    g0: LineSegment [constr] StartX=-16.5338 StartY=-4.1 StartZ=0 EndX=20.0569 EndY=-4.1 EndZ=0
    g1: LineSegment StartX=-12.2048 StartY=0 StartZ=0 EndX=-12.2048 EndY=-4.1 EndZ=0
    g2: LineSegment StartX=-12.2048 StartY=-4.1 StartZ=0 EndX=-5 EndY=-4.1 EndZ=0
    g3: LineSegment StartX=-5 StartY=-4.1 StartZ=0 EndX=-5 EndY=-2.6 EndZ=0
    g4: LineSegment StartX=-5 StartY=-2.6 StartZ=0 EndX=5 EndY=-2.6 EndZ=0
    g5: LineSegment StartX=5 StartY=-2.6 StartZ=0 EndX=5 EndY=-4.1 EndZ=0
    g6: LineSegment StartX=5 StartY=-4.1 StartZ=0 EndX=12.1026 EndY=-4.1 EndZ=0
    g7: LineSegment StartX=12.1026 StartY=-4.1 StartZ=0 EndX=12.1026 EndY=0 EndZ=0
    g8: LineSegment StartX=12.1026 StartY=0 StartZ=0 EndX=-12.2048 EndY=0 EndZ=0
  constraints (23):
    c: Horizontal(g0)
    c: DistanceY(g0,g-1) = 4.1
    c: PointOnObject(g1,g-1)
    c: PointOnObject(g1,g0)
    c: Coincident(g1,g2)
    c: PointOnObject(g2,g0)
    c: Coincident(g2,g3)
    c: Vertical(g3)
    c: Coincident(g3,g4)
    c: Coincident(g4,g5)
    c: PointOnObject(g5,g0)
    c: Coincident(g5,g6)
    c: PointOnObject(g6,g0)
    c: Coincident(g6,g7)
    c: PointOnObject(g7,g-1)
    c: Coincident(g7,g8)
    c: Coincident(g8,g1)
    c: Vertical(g5)
    c: Vertical(g7)
    c: Vertical(g1)
    c: DistanceY(g4,g-1) = 2.6
    c: DistanceX(g2,g5) = 10
    c: Symmetric(g4,g3,g-2)
FEATURE [PartDesign::Revolution] Revolution
  Angle = 360
  Axis = (1,0,0)
  Base = (0,0,0)
  Placement = pos=(0,0,0) rot=(1,0,0;1.5708rad)
  Profile = -> Sketch023
  ReferenceAxis = -> Sketch023 [H_Axis]
  Reversed = true
FEATURE [PartDesign::Body] Body033  label="schwinge-bohung-innen"
  Group = -> [Sketch023,Revolution]
  Origin = -> Origin052
  Placement = pos=(0,-17.1,-12) rot=(0,0,1;0rad)
  Tip = -> Revolution
FEATURE [Part::Cut] Cut062
  Base = -> Body031
  Tool = -> Body033
FEATURE [Part::Cut] Cut063
  Base = -> Cut062
  Tool = -> Cylinder069
FEATURE [Part::Cut] Cut064
  Base = -> Cut063
  Tool = -> Body032
FEATURE [App::DocumentObjectGroup] Group016  label="ausnehmungen"
  Group = -> [Cut064]
FEATURE [App::DocumentObjectGroup] Group015  label="kardan"
  Group = -> [Group016]
FEATURE [App::Part] Part015  label="kardan-gelenk"
  Group = -> [Group014,Body028,Body029,Body030,Cylinder068,Group015,Body031,Cylinder069,Body032,Group016,Body033,Cut062,Cut063,Cut064]
  Origin = -> Origin046
  Placement = pos=(36.4481,-22.1668,16.5) rot=(0,0,1;6.10865rad)
FEATURE [App::DocumentObjectGroup] Gruppe010  label="kardan001"
FEATURE [Sketcher::SketchObject] Sketch027
  MapMode = 5
  Placement = pos=(0,0,0) rot=(1,0,0;1.5708rad)
  Support = -> [XZ_Plane060]
  sketch-geometry (9):
    g0: LineSegment [constr] StartX=-16.5338 StartY=-4.1 StartZ=0 EndX=20.0569 EndY=-4.1 EndZ=0
    g1: LineSegment StartX=-14.3364 StartY=0 StartZ=0 EndX=-14.3364 EndY=-4.1 EndZ=0
    g2: LineSegment StartX=-14.3364 StartY=-4.1 StartZ=0 EndX=-5 EndY=-4.1 EndZ=0
    g3: LineSegment StartX=-5 StartY=-4.1 StartZ=0 EndX=-5 EndY=-2.6 EndZ=0
    g4: LineSegment StartX=-5 StartY=-2.6 StartZ=0 EndX=5 EndY=-2.6 EndZ=0
    g5: LineSegment StartX=5 StartY=-2.6 StartZ=0 EndX=5 EndY=-4.1 EndZ=0
    g6: LineSegment StartX=5 StartY=-4.1 StartZ=0 EndX=16.0338 EndY=-4.1 EndZ=0
    g7: LineSegment StartX=16.0338 StartY=-4.1 StartZ=0 EndX=16.0338 EndY=0 EndZ=0
    g8: LineSegment StartX=16.0338 StartY=0 StartZ=0 EndX=-14.3364 EndY=0 EndZ=0
  constraints (23):
    c: Horizontal(g0)
    c: DistanceY(g0,g-1) = 4.1
    c: PointOnObject(g1,g-1)
    c: PointOnObject(g1,g0)
    c: Coincident(g1,g2)
    c: PointOnObject(g2,g0)
    c: Coincident(g2,g3)
    c: Vertical(g3)
    c: Coincident(g3,g4)
    c: Coincident(g4,g5)
    c: PointOnObject(g5,g0)
    c: Coincident(g5,g6)
    c: PointOnObject(g6,g0)
    c: Coincident(g6,g7)
    c: PointOnObject(g7,g-1)
    c: Coincident(g7,g8)
    c: Coincident(g8,g1)
    c: Vertical(g5)
    c: Vertical(g7)
    c: Vertical(g1)
    c: DistanceY(g4,g-1) = 2.6
    c: DistanceX(g2,g5) = 10
    c: Symmetric(g4,g3,g-2)
FEATURE [Sketcher::SketchObject] Sketch028
  MapMode = 5
  Placement = pos=(0,0,0) rot=(1,0,0;1.5708rad)
  Support = -> [XZ_Plane061]
  sketch-geometry (18):
    g0: LineSegment [constr] StartX=-20.0973 StartY=-50 StartZ=0 EndX=19.8963 EndY=-50 EndZ=0
    g1: Circle [constr] CenterX=0 CenterY=12 CenterZ=0 NormalX=0 NormalY=0 NormalZ=1 AngleXU=0 Radius=2.5
    g2: LineSegment [constr] StartX=-5.73448 StartY=12 StartZ=0 EndX=5.42277 EndY=12 EndZ=0
    g3: LineSegment [constr] StartX=-21.793 StartY=-16 StartZ=0 EndX=21.3873 EndY=-16 EndZ=0
    g4: LineSegment [constr] StartX=-3.5 StartY=1.62024 StartZ=0 EndX=-3.5 EndY=-60.1026 EndZ=0
    g5: LineSegment [constr] StartX=3.5 StartY=1.62024 StartZ=0 EndX=3.5 EndY=-59.0889 EndZ=0
    g6: ArcOfCircle CenterX=0 CenterY=12 CenterZ=0 NormalX=0 NormalY=0 NormalZ=1 AngleXU=0 Radius=23.7592 StartAngle=4.56454 EndAngle=4.86024
    g7: LineSegment StartX=-3.5 StartY=-11.5 StartZ=0 EndX=-3.5 EndY=-20.5 EndZ=0
    g8: LineSegment StartX=-3.5 StartY=-20.5 StartZ=0 EndX=3.5 EndY=-20.5 EndZ=0
    g9: LineSegment StartX=3.5 StartY=-20.5 StartZ=0 EndX=3.5 EndY=-11.5 EndZ=0
    g10: LineSegment [constr] StartX=-17.0948 StartY=-14.5 StartZ=0 EndX=19.2666 EndY=-14.5 EndZ=0
    g11: LineSegment [constr] StartX=19.2666 StartY=-14.5 StartZ=0 EndX=19.2666 EndY=-17.5 EndZ=0
    g12: LineSegment [constr] StartX=19.2666 StartY=-17.5 StartZ=0 EndX=-17.0948 EndY=-17.5 EndZ=0
    g13: LineSegment [constr] StartX=-17.0948 StartY=-17.5 StartZ=0 EndX=-17.0948 EndY=-14.5 EndZ=0
    g14: LineSegment [constr] StartX=-16.9815 StartY=1.5 StartZ=0 EndX=19.1534 EndY=1.5 EndZ=0
    g15: LineSegment [constr] StartX=19.1534 StartY=1.5 StartZ=0 EndX=19.1534 EndY=-1.5 EndZ=0
    g16: LineSegment [constr] StartX=19.1534 StartY=-1.5 StartZ=0 EndX=-16.9815 EndY=-1.5 EndZ=0
    g17: LineSegment [constr] StartX=-16.9815 StartY=-1.5 StartZ=0 EndX=-16.9815 EndY=1.5 EndZ=0
  constraints (43):
    c: Horizontal(g0)
    c: DistanceY(g0,g-1) = 50
    c: PointOnObject(g1,g-2)
    c: Radius(g1) = 2.5
    c: Horizontal(g2)
    c: PointOnObject(g1,g2)
    c: DistanceY(g-1,g2) = 12
    c: Horizontal(g3)
    c: DistanceY(g3,g-1) = 16
    c: Vertical(g4)
    c: Vertical(g5)
    c: DistanceX(g4,g5) = 7
    c: Symmetric(g4,g5,g-2)
    c: Coincident(g6,g1)
    c: PointOnObject(g6,g4)
    c: PointOnObject(g6,g5)
    c: DistanceY(g6,g-1) = 11.5
    c: Coincident(g6,g7)
    c: Coincident(g7,g8)
    c: Horizontal(g8)
    c: Coincident(g8,g9)
    c: Coincident(g9,g6)
    c: PointOnObject(g8,g5)
    c: PointOnObject(g7,g4)
    c: Coincident(g10,g11)
    c: Coincident(g11,g12)
    c: Coincident(g12,g13)
    c: Coincident(g13,g10)
    c: Horizontal(g10)
    c: Horizontal(g12)
    c: Vertical(g13)
    c: Symmetric(g11,g10,g3)
    c: DistanceY(g8,g6) = 9
    c: Coincident(g14,g15)
    c: Coincident(g15,g16)
    c: Coincident(g16,g17)
    c: Coincident(g17,g14)
    c: Horizontal(g14)
    c: Horizontal(g16)
    c: Vertical(g17)
    c: Symmetric(g15,g14,g-1)
    c: DistanceY(g12,g10) = 3
    c: DistanceY(g16,g14) = 3
FEATURE [PartDesign::Body] Body040  label="blech_0"
  Group = -> [Sketch028]
  Origin = -> Origin060
  Placement = pos=(0,-17.1,-12) rot=(0,0,1;0rad)
FEATURE [Sketcher::SketchObject] Sketch029
  AttachmentOffset = pos=(0,0,0) rot=(0,1,0;1.5708rad)
  MapMode = 5
  Placement = pos=(0,0,0) rot=(0.57735,0.57735,0.57735;2.0944rad)
  Support = -> [XZ_Plane062]
  sketch-geometry (17):
    g0: LineSegment [constr] StartX=-16.5338 StartY=-52 StartZ=0 EndX=20.0569 EndY=-52 EndZ=0
    g1: LineSegment StartX=-5.98289 StartY=-27.7265 StartZ=0 EndX=-16.5781 EndY=-33.2872 EndZ=0
    g2: LineSegment StartX=-16.5781 StartY=-33.2872 StartZ=0 EndX=-23.3754 EndY=-43.1349 EndZ=0
    g3: LineSegment StartX=-23.3754 StartY=-43.1349 StartZ=0 EndX=-24.8177 EndY=-55.0134 EndZ=0
    g4: LineSegment StartX=-24.8177 StartY=-55.0134 StartZ=0 EndX=-20.5746 EndY=-66.2016 EndZ=0
    g5: LineSegment StartX=-20.5746 StartY=-66.2016 StartZ=0 EndX=-11.6181 EndY=-74.1364 EndZ=0
    g6: LineSegment StartX=-11.6181 StartY=-74.1364 StartZ=0 EndX=1.8e-15 EndY=-77 EndZ=0
    g7: LineSegment StartX=1.8e-15 StartY=-77 StartZ=0 EndX=11.6181 EndY=-74.1364 EndZ=0
    g8: LineSegment StartX=11.6181 StartY=-74.1364 StartZ=0 EndX=20.5746 EndY=-66.2016 EndZ=0
    g9: LineSegment StartX=20.5746 StartY=-66.2016 StartZ=0 EndX=24.8177 EndY=-55.0134 EndZ=0
    g10: LineSegment StartX=24.8177 StartY=-55.0134 StartZ=0 EndX=23.3754 EndY=-43.1349 EndZ=0
    g11: LineSegment StartX=23.3754 StartY=-43.1349 StartZ=0 EndX=16.5781 EndY=-33.2872 EndZ=0
    g12: LineSegment StartX=16.5781 StartY=-33.2872 StartZ=0 EndX=5.98289 EndY=-27.7265 EndZ=0
    g13: LineSegment StartX=5.98289 StartY=-27.7265 StartZ=0 EndX=-5.98289 EndY=-27.7265 EndZ=0
    g14: Circle [constr] CenterX=0 CenterY=-52 CenterZ=0 NormalX=0 NormalY=0 NormalZ=1 AngleXU=0 Radius=25
    g15: Circle CenterX=0 CenterY=-52 CenterZ=0 NormalX=0 NormalY=0 NormalZ=1 AngleXU=0 Radius=4
    g16: LineSegment [constr] StartX=-22.8748 StartY=-17 StartZ=0 EndX=37.2668 EndY=-17 EndZ=0
  constraints (37):
    c: Horizontal(g0)
    c: Coincident(g1,g2)
    c: Coincident(g2,g3)
    c: Coincident(g3,g4)
    c: Coincident(g4,g5)
    c: Coincident(g5,g6)
    c: Coincident(g6,g7)
    c: Coincident(g7,g8)
    c: Coincident(g8,g9)
    c: Coincident(g9,g10)
    c: Coincident(g10,g11)
    c: Coincident(g11,g12)
    c: Coincident(g12,g13)
    c: Coincident(g13,g1)
    c: Equal(g1, g2-g13) x12
    c: PointOnObject(g1,g14)
    c: PointOnObject(g2,g14)
    c: PointOnObject(g3,g14)
    c: PointOnObject(g4,g14)
    c: PointOnObject(g5,g14)
    c: PointOnObject(g6,g14)
    c: PointOnObject(g7,g14)
    c: PointOnObject(g8,g14)
    c: PointOnObject(g9,g14)
    c: PointOnObject(g10,g14)
    c: PointOnObject(g11,g14)
    c: PointOnObject(g12,g14)
    c: PointOnObject(g13,g14)
    c: PointOnObject(g14,g0)
    c: Horizontal(g13)
    c: PointOnObject(g14,g-2)
    c: Radius(g14) = 25
    c: DistanceY(g0,g-1) = 52
    c: Coincident(g15,g14)
    c: Radius(g15) = 4
    c: Horizontal(g16)
    c: DistanceY(g16,g-1) = 17
FEATURE [PartDesign::Pad] Pad023
  Length = 5.6
  Length2 = 100
  Placement = pos=(0,0,0) rot=(1,0,0;1.5708rad)
  Profile = -> Sketch029
  Type = 0
FEATURE [PartDesign::Body] Body041  label="zahn-rad"
  Group = -> [Sketch029,Pad023]
  Origin = -> Origin061
  Placement = pos=(-2.8,-17.1,-12) rot=(0,0,1;0rad)
  Tip = -> Pad023
FEATURE [Sketcher::SketchObject] Sketch031
  AttachmentOffset = pos=(0,0,0) rot=(0,1,0;1.5708rad)
  MapMode = 5
  Placement = pos=(0,0,0) rot=(0.57735,0.57735,0.57735;2.0944rad)
  Support = -> [XZ_Plane064]
  sketch-geometry (4):
    g0: LineSegment [constr] StartX=-27.0262 StartY=-52 StartZ=0 EndX=32.4684 EndY=-52 EndZ=0
    g1: Circle CenterX=0 CenterY=-52 CenterZ=0 NormalX=0 NormalY=0 NormalZ=1 AngleXU=0 Radius=3.9
    g2: Circle CenterX=0 CenterY=-52 CenterZ=0 NormalX=0 NormalY=0 NormalZ=1 AngleXU=0 Radius=2.5
    g3: LineSegment [constr] StartX=-21.8612 StartY=-17 StartZ=0 EndX=42.2223 EndY=-17 EndZ=0
  constraints (9):
    c: Horizontal(g0)
    c: DistanceY(g0,g-1) = 52
    c: PointOnObject(g1,g0)
    c: PointOnObject(g1,g-2)
    c: Radius(g1) = 3.9
    c: Coincident(g2,g1)
    c: Radius(g2) = 2.5
    c: Horizontal(g3)
    c: DistanceY(g3,g-1) = 17
FEATURE [PartDesign::Pad] Pad024
  Length = 7
  Length2 = 100
  Placement = pos=(0,0,0) rot=(1,0,0;1.5708rad)
  Profile = -> Sketch031
  Type = 0
FEATURE [PartDesign::Body] Body043  label="rad_hülse"
  Group = -> [Sketch031,Pad024]
  Origin = -> Origin063
  Placement = pos=(-3.5,-17.1,-12) rot=(0,0,1;0rad)
  Tip = -> Pad024
FEATURE [Sketcher::SketchObject] Sketch032
  MapMode = 5
  Placement = pos=(0,0,0) rot=(1,0,0;1.5708rad)
  Support = -> [XZ_Plane065]
  sketch-geometry (2):
    g0: LineSegment [constr] StartX=-20.0973 StartY=-52 StartZ=0 EndX=19.8963 EndY=-52 EndZ=0
    g1: LineSegment [constr] StartX=-20.4732 StartY=-16 StartZ=0 EndX=19.2834 EndY=-16 EndZ=0
  constraints (4):
    c: Horizontal(g0)
    c: DistanceY(g0,g-1) = 52
    c: Horizontal(g1)
    c: DistanceY(g1,g-1) = 16
FEATURE [PartDesign::Body] Body044  label="distance_0"
  Group = -> [Sketch032]
  Origin = -> Origin064
  Placement = pos=(0,-17.1,-12) rot=(0,0,1;0rad)
FEATURE [PartDesign::Revolution] Revolution007
  Angle = 360
  Axis = (1,0,0)
  Base = (0,0,0)
  Placement = pos=(0,0,0) rot=(1,0,0;1.5708rad)
  Profile = -> Sketch027
  ReferenceAxis = -> Sketch027 [H_Axis]
  Reversed = true
FEATURE [PartDesign::Body] Body039  label="schwinge-bohung-innen001"
  Group = -> [Sketch027,Revolution007]
  Origin = -> Origin059
  Placement = pos=(0,-17.1,-12) rot=(0,0,1;0rad)
  Tip = -> Revolution007
FEATURE [App::DocumentObjectGroup] Group018  label="welle"
  Group = -> [Body039]
FEATURE [Sketcher::SketchObject] Sketch033
  AttachmentOffset = pos=(0,0,0) rot=(0,1,0;1.5708rad)
  MapMode = 5
  Placement = pos=(0,0,0) rot=(0.57735,0.57735,0.57735;2.0944rad)
  Support = -> [XZ_Plane066]
  sketch-geometry (22):
    g0: LineSegment [constr] StartX=-27.0262 StartY=-52 StartZ=0 EndX=32.4684 EndY=-52 EndZ=0
    g1: LineSegment [constr] StartX=-26.5915 StartY=-17 StartZ=0 EndX=27.3559 EndY=-17 EndZ=0
    g2: Circle [constr] CenterX=0 CenterY=0 CenterZ=0 NormalX=0 NormalY=0 NormalZ=1 AngleXU=0 Radius=1.75
    g3: ArcOfCircle CenterX=0 CenterY=0 CenterZ=0 NormalX=0 NormalY=0 NormalZ=1 AngleXU=0 Radius=13 StartAngle=4.15032 EndAngle=5.27446
    g4: LineSegment [constr] StartX=-7.5 StartY=2.28754 StartZ=0 EndX=-7.5 EndY=-32.4888 EndZ=0
    g5: LineSegment [constr] StartX=7.5 StartY=2.51533 StartZ=0 EndX=7.5 EndY=-32.4888 EndZ=0
    g6: LineSegment [constr] StartX=-14.4286 StartY=-11 StartZ=0 EndX=14.1973 EndY=-11 EndZ=0
    g7: ArcOfCircle CenterX=0 CenterY=-52 CenterZ=0 NormalX=0 NormalY=0 NormalZ=1 AngleXU=0 Radius=30 StartAngle=1.3524 EndAngle=1.7892
    g8: LineSegment [constr] StartX=-2.4e-15 StartY=-22 StartZ=0 EndX=-2.4e-15 EndY=-13 EndZ=0
    g9: LineSegment [constr] StartX=-12.2452 StartY=-22.7126 StartZ=0 EndX=11.7489 EndY=-22.7126 EndZ=0
    g10: LineSegment [constr] StartX=-4 StartY=-12.5552 StartZ=0 EndX=-4 EndY=-18.9221 EndZ=0
    g11: LineSegment [constr] StartX=4 StartY=-12.707 StartZ=0 EndX=4 EndY=-18.9221 EndZ=0
    g12: Circle CenterX=-4 CenterY=-17 CenterZ=0 NormalX=0 NormalY=0 NormalZ=1 AngleXU=0 Radius=2.2
    g13: Circle CenterX=4 CenterY=-17 CenterZ=0 NormalX=0 NormalY=0 NormalZ=1 AngleXU=0 Radius=2.2
    g14: LineSegment StartX=-6.9282 StartY=-11 StartZ=0 EndX=-7.5 EndY=-11 EndZ=0
    g15: LineSegment StartX=-7.5 StartY=-11 StartZ=0 EndX=-7.5 EndY=-22.7126 EndZ=0
    g16: LineSegment StartX=-7.5 StartY=-22.7126 StartZ=0 EndX=-6.5 EndY=-22.7126 EndZ=0
    g17: LineSegment StartX=6.9282 StartY=-11 StartZ=0 EndX=7.5 EndY=-11 EndZ=0
    g18: LineSegment StartX=7.5 StartY=-11 StartZ=0 EndX=7.5 EndY=-22.7126 EndZ=0
    g19: LineSegment StartX=7.5 StartY=-22.7126 StartZ=0 EndX=6.5 EndY=-22.7126 EndZ=0
    g20: LineSegment [constr] StartX=-10.7708 StartY=-20 StartZ=0 EndX=12.7401 EndY=-20 EndZ=0
    g21: Circle CenterX=-2.4e-15 CenterY=-20 CenterZ=0 NormalX=0 NormalY=0 NormalZ=1 AngleXU=0 Radius=1.1
  constraints (57):
    c: Horizontal(g0)
    c: DistanceY(g0,g-1) = 52
    c: Horizontal(g1)
    c: DistanceY(g1,g-1) = 17
    c: Coincident(g2,g-1)
    c: Radius(g2) = 1.75
    c: Coincident(g3,g-1)
    c: Vertical(g4)
    c: Vertical(g5)
    c: DistanceX(g4,g5) = 15
    c: Symmetric(g5,g4,g-2)
    c: Horizontal(g6)
    c: Radius(g3) = 13
    c: PointOnObject(g3,g6)
    c: PointOnObject(g3,g6)
    c: PointOnObject(g7,g-2)
    c: PointOnObject(g7,g0)
    c: Vertical(g8)
    c: Perpendicular(g8,g3) = 4.71239
    c: DistanceY(g8,g8) = 9
    c: PointOnObject(g8,g7)
    c: Horizontal(g9)
    c: PointOnObject(g7,g9)
    c: PointOnObject(g7,g9)
    c: DistanceX(g7,g7) = 13
    c: Vertical(g10)
    c: Vertical(g11)
    c: Symmetric(g10,g11,g-2)
    c: DistanceX(g11,g5) = 3.5
    c: PointOnObject(g12,g10)
    c: PointOnObject(g13,g11)
    c: PointOnObject(g13,g1)
    c: PointOnObject(g12,g1)
    c: Radius(g12) = 2.2
    c: Radius(g13) = 2.2
    c: Horizontal(g14)
    c: Coincident(g14,g15)
    c: Vertical(g15)
    c: Coincident(g15,g16)
    c: Horizontal(g16)
    c: Coincident(g17,g18)
    c: Vertical(g18)
    c: Coincident(g18,g19)
    c: Horizontal(g17)
    c: Horizontal(g19)
    c: Coincident(g14,g3)
    c: Coincident(g17,g3)
    c: Coincident(g7,g19)
    c: Coincident(g16,g7)
    c: PointOnObject(g15,g4)
    c: PointOnObject(g18,g5)
    c: DistanceY(g6,g3) = 11
    c: Horizontal(g20)
    c: DistanceY(g20,g1) = 3
    c: PointOnObject(g21,g8)
    c: PointOnObject(g21,g20)
    c: Radius(g21) = 1.1
FEATURE [PartDesign::Pad] Pad025
  Length = 9
  Length2 = 100
  Placement = pos=(0,0,0) rot=(1,0,0;1.5708rad)
  Profile = -> Sketch033
  Type = 0
FEATURE [PartDesign::Body] Body045  label="distance_innen"
  Group = -> [Sketch033,Pad025]
  Origin = -> Origin065
  Placement = pos=(-4.5,-17.1,-12) rot=(0,0,1;0rad)
  Tip = -> Pad025
FEATURE [Sketcher::SketchObject] Sketch034
  AttachmentOffset = pos=(0,0,0) rot=(0,1,0;1.5708rad)
  MapMode = 5
  Placement = pos=(0,0,0) rot=(0.57735,0.57735,0.57735;2.0944rad)
  Support = -> [XZ_Plane067]
  sketch-geometry (12):
    g0: LineSegment [constr] StartX=-27.0262 StartY=-52 StartZ=0 EndX=32.4684 EndY=-52 EndZ=0
    g1: LineSegment [constr] StartX=-26.5915 StartY=-17 StartZ=0 EndX=27.3559 EndY=-17 EndZ=0
    g2: Circle [constr] CenterX=0 CenterY=0 CenterZ=0 NormalX=0 NormalY=0 NormalZ=1 AngleXU=0 Radius=1.75
    g3: LineSegment [constr] StartX=-7.5 StartY=2.28754 StartZ=0 EndX=-7.5 EndY=-32.4888 EndZ=0
    g4: LineSegment [constr] StartX=7.5 StartY=2.51533 StartZ=0 EndX=7.5 EndY=-32.4888 EndZ=0
    g5: LineSegment [constr] StartX=-14.793 StartY=-11.2588 StartZ=0 EndX=13.8329 EndY=-11.2588 EndZ=0
    g6: LineSegment [constr] StartX=-2.4e-15 StartY=-22 StartZ=0 EndX=-2.4e-15 EndY=-13 EndZ=0
    g7: LineSegment [constr] StartX=-12.2452 StartY=-22.7126 StartZ=0 EndX=11.7489 EndY=-22.7126 EndZ=0
    g8: LineSegment [constr] StartX=-4 StartY=-12.5552 StartZ=0 EndX=-4 EndY=-18.9221 EndZ=0
    g9: LineSegment [constr] StartX=4 StartY=-12.707 StartZ=0 EndX=4 EndY=-18.9221 EndZ=0
    g10: Circle CenterX=-4 CenterY=-17 CenterZ=0 NormalX=0 NormalY=0 NormalZ=1 AngleXU=0 Radius=1.75
    g11: Circle CenterX=4 CenterY=-17 CenterZ=0 NormalX=0 NormalY=0 NormalZ=1 AngleXU=0 Radius=1.75
  constraints (23):
    c: Horizontal(g0)
    c: DistanceY(g0,g-1) = 52
    c: Horizontal(g1)
    c: DistanceY(g1,g-1) = 17
    c: Coincident(g2,g-1)
    c: Radius(g2) = 1.75
    c: Vertical(g3)
    c: Vertical(g4)
    c: DistanceX(g3,g4) = 15
    c: Symmetric(g4,g3,g-2)
    c: Horizontal(g5)
    c: Vertical(g6)
    c: Horizontal(g7)
    c: Vertical(g8)
    c: Vertical(g9)
    c: Symmetric(g8,g9,g-2)
    c: DistanceX(g9,g4) = 3.5
    c: PointOnObject(g10,g8)
    c: PointOnObject(g11,g9)
    c: PointOnObject(g11,g1)
    c: PointOnObject(g10,g1)
    c: Radius(g10) = 1.75
    c: Radius(g11) = 1.75
FEATURE [PartDesign::Body] Body046  label="blech_muster"
  Group = -> [Sketch034]
  Origin = -> Origin066
  Placement = pos=(-3.5,-17.1,-12) rot=(0,0,1;0rad)
FEATURE [Sketcher::SketchObject] Sketch035
  AttachmentOffset = pos=(0,0,0) rot=(0,1,0;1.5708rad)
  MapMode = 5
  Placement = pos=(0,0,0) rot=(0.57735,0.57735,0.57735;2.0944rad)
  Support = -> [XZ_Plane068]
  sketch-geometry (23):
    g0: LineSegment [constr] StartX=-27.0262 StartY=-52 StartZ=0 EndX=32.4684 EndY=-52 EndZ=0
    g1: LineSegment [constr] StartX=-26.5915 StartY=-17 StartZ=0 EndX=27.3559 EndY=-17 EndZ=0
    g2: Circle [constr] CenterX=0 CenterY=0 CenterZ=0 NormalX=0 NormalY=0 NormalZ=1 AngleXU=0 Radius=1.75
    g3: LineSegment [constr] StartX=-7.5 StartY=2.28754 StartZ=0 EndX=-7.5 EndY=-69.1543 EndZ=0
    g4: LineSegment [constr] StartX=7.5 StartY=2.51533 StartZ=0 EndX=7.5 EndY=-69.1543 EndZ=0
    g5: LineSegment [constr] StartX=-14.793 StartY=-11 StartZ=0 EndX=13.8329 EndY=-11 EndZ=0
    g6: LineSegment [constr] StartX=-2.4e-15 StartY=-22 StartZ=0 EndX=-2.4e-15 EndY=-13 EndZ=0
    g7: LineSegment [constr] StartX=-12.2452 StartY=-35 StartZ=0 EndX=11.5457 EndY=-35 EndZ=0
    g8: LineSegment [constr] StartX=-4 StartY=-12.5552 StartZ=0 EndX=-4 EndY=-18.9221 EndZ=0
    g9: LineSegment [constr] StartX=4 StartY=-12.707 StartZ=0 EndX=4 EndY=-18.9221 EndZ=0
    g10: Circle CenterX=-4 CenterY=-17 CenterZ=0 NormalX=0 NormalY=0 NormalZ=1 AngleXU=0 Radius=2.1
    g11: Circle CenterX=4 CenterY=-17 CenterZ=0 NormalX=0 NormalY=0 NormalZ=1 AngleXU=0 Radius=2.1
    g12: ArcOfCircle CenterX=0 CenterY=0 CenterZ=0 NormalX=0 NormalY=0 NormalZ=1 AngleXU=0 Radius=13 StartAngle=4.15032 EndAngle=5.27446
    g13: LineSegment [constr] StartX=-26.6334 StartY=-65 StartZ=0 EndX=31.186 EndY=-65 EndZ=0
    g14: LineSegment StartX=-6.9282 StartY=-11 StartZ=0 EndX=-7.5 EndY=-11 EndZ=0
    g15: LineSegment StartX=-7.5 StartY=-11 StartZ=0 EndX=-7.5 EndY=-65 EndZ=0
    g16: LineSegment StartX=-7.5 StartY=-65 StartZ=0 EndX=7.5 EndY=-65 EndZ=0
    g17: LineSegment StartX=7.5 StartY=-65 StartZ=0 EndX=7.5 EndY=-11 EndZ=0
    g18: LineSegment StartX=7.5 StartY=-11 StartZ=0 EndX=6.9282 EndY=-11 EndZ=0
    g19: Circle CenterX=0 CenterY=-52 CenterZ=0 NormalX=0 NormalY=0 NormalZ=1 AngleXU=0 Radius=2.5
    g20: Circle CenterX=0 CenterY=-35 CenterZ=0 NormalX=0 NormalY=0 NormalZ=1 AngleXU=0 Radius=2.1
    g21: LineSegment [constr] StartX=-9.81744 StartY=-20 StartZ=0 EndX=10.5694 EndY=-20 EndZ=0
    g22: Circle CenterX=-2.4e-15 CenterY=-20 CenterZ=0 NormalX=0 NormalY=0 NormalZ=1 AngleXU=0 Radius=1.1
  constraints (56):
    c: Horizontal(g0)
    c: DistanceY(g0,g-1) = 52
    c: Horizontal(g1)
    c: DistanceY(g1,g-1) = 17
    c: Coincident(g2,g-1)
    c: Radius(g2) = 1.75
    c: Vertical(g3)
    c: Vertical(g4)
    c: DistanceX(g3,g4) = 15
    c: Symmetric(g4,g3,g-2)
    c: Horizontal(g5)
    c: Vertical(g6)
    c: Horizontal(g7)
    c: Vertical(g8)
    c: Vertical(g9)
    c: Symmetric(g8,g9,g-2)
    c: DistanceX(g9,g4) = 3.5
    c: PointOnObject(g10,g8)
    c: PointOnObject(g11,g9)
    c: PointOnObject(g11,g1)
    c: PointOnObject(g10,g1)
    c: Radius(g10) = 2.1
    c: Radius(g11) = 2.1
    c: DistanceY(g5,g-1) = 11
    c: Coincident(g12,g-1)
    c: PointOnObject(g12,g5)
    c: PointOnObject(g12,g5)
    c: Radius(g12) = 13
    c: Horizontal(g13)
    c: Coincident(g14,g15)
    c: PointOnObject(g15,g13)
    c: Vertical(g15)
    c: Coincident(g15,g16)
    c: PointOnObject(g16,g13)
    c: Coincident(g16,g17)
    c: Vertical(g17)
    c: Coincident(g17,g18)
    c: Horizontal(g18)
    c: Coincident(g18,g12)
    c: Horizontal(g14)
    c: Coincident(g14,g12)
    c: PointOnObject(g16,g4)
    c: PointOnObject(g15,g3)
    c: DistanceY(g13,g5) = 54
    c: PointOnObject(g19,g-2)
    c: PointOnObject(g19,g0)
    c: Radius(g19) = 2.5
    c: DistanceY(g13,g7) = 30
    c: PointOnObject(g20,g-2)
    c: PointOnObject(g20,g7)
    c: Radius(g20) = 2.1
    c: Horizontal(g21)
    c: DistanceY(g21,g1) = 3
    c: PointOnObject(g22,g6)
    c: PointOnObject(g22,g21)
    c: Radius(g22) = 1.1
FEATURE [PartDesign::Pad] Pad026
  Length = 3
  Length2 = 100
  Placement = pos=(0,0,0) rot=(1,0,0;1.5708rad)
  Profile = -> Sketch035
  Type = 0
FEATURE [PartDesign::Body] Body047  label="blech_innen_L"
  Group = -> [Sketch035,Pad026]
  Origin = -> Origin067
  Placement = pos=(-7.5,-17.1,-12) rot=(0,0,1;0rad)
  Tip = -> Pad026
FEATURE [Sketcher::SketchObject] Sketch037
  AttachmentOffset = pos=(0,0,0) rot=(0,1,0;1.5708rad)
  MapMode = 5
  Placement = pos=(0,0,0) rot=(0.57735,0.57735,0.57735;2.0944rad)
  Support = -> [XZ_Plane070]
  sketch-geometry (4):
    g0: LineSegment [constr] StartX=-27.0262 StartY=-52 StartZ=0 EndX=32.4684 EndY=-52 EndZ=0
    g1: Circle CenterX=0 CenterY=-52 CenterZ=0 NormalX=0 NormalY=0 NormalZ=1 AngleXU=0 Radius=9
    g2: Circle CenterX=0 CenterY=-52 CenterZ=0 NormalX=0 NormalY=0 NormalZ=1 AngleXU=0 Radius=2.5
    g3: LineSegment [constr] StartX=-21.8612 StartY=-17 StartZ=0 EndX=42.2223 EndY=-17 EndZ=0
  constraints (9):
    c: Horizontal(g0)
    c: DistanceY(g0,g-1) = 52
    c: PointOnObject(g1,g0)
    c: PointOnObject(g1,g-2)
    c: Radius(g1) = 9
    c: Coincident(g2,g1)
    c: Radius(g2) = 2.5
    c: Horizontal(g3)
    c: DistanceY(g3,g-1) = 17
FEATURE [PartDesign::Pad] Pad027
  Length = 1
  Length2 = 100
  Placement = pos=(0,0,0) rot=(1,0,0;1.5708rad)
  Profile = -> Sketch037
  Type = 0
FEATURE [PartDesign::Body] Body049  label="scheibe_L"
  Group = -> [Sketch037,Pad027]
  Origin = -> Origin069
  Placement = pos=(-4,-17.1,-12) rot=(0,0,1;0rad)
  Tip = -> Pad027
FEATURE [Sketcher::SketchObject] Sketch038
  AttachmentOffset = pos=(0,0,0) rot=(0,1,0;1.5708rad)
  MapMode = 5
  Placement = pos=(0,0,0) rot=(0.57735,0.57735,0.57735;2.0944rad)
  Support = -> [XZ_Plane071]
  sketch-geometry (4):
    g0: LineSegment [constr] StartX=-27.0262 StartY=-52 StartZ=0 EndX=32.4684 EndY=-52 EndZ=0
    g1: Circle CenterX=0 CenterY=-52 CenterZ=0 NormalX=0 NormalY=0 NormalZ=1 AngleXU=0 Radius=9
    g2: Circle CenterX=0 CenterY=-52 CenterZ=0 NormalX=0 NormalY=0 NormalZ=1 AngleXU=0 Radius=2.5
    g3: LineSegment [constr] StartX=-21.8612 StartY=-17 StartZ=0 EndX=42.2223 EndY=-17 EndZ=0
  constraints (9):
    c: Horizontal(g0)
    c: DistanceY(g0,g-1) = 52
    c: PointOnObject(g1,g0)
    c: PointOnObject(g1,g-2)
    c: Radius(g1) = 9
    c: Coincident(g2,g1)
    c: Radius(g2) = 2.5
    c: Horizontal(g3)
    c: DistanceY(g3,g-1) = 17
FEATURE [PartDesign::Pad] Pad028
  Length = 1
  Length2 = 100
  Placement = pos=(0,0,0) rot=(1,0,0;1.5708rad)
  Profile = -> Sketch038
  Type = 0
FEATURE [PartDesign::Body] Body050  label="scheibe_R"
  Group = -> [Sketch038,Pad028]
  Origin = -> Origin070
  Placement = pos=(3.5,-17.1,-12) rot=(0,0,1;0rad)
  Tip = -> Pad028
FEATURE [App::DocumentObjectGroup] Gruppe011  label="scheiben_F"
  Group = -> [Body049,Body050]
FEATURE [App::DocumentObjectGroup] Group022  label="zahn_satz_F"
  Group = -> [Body041,Body043,Gruppe011]
FEATURE [Sketcher::SketchObject] Sketch039
  AttachmentOffset = pos=(0,0,0) rot=(0,1,0;1.5708rad)
  MapMode = 5
  Placement = pos=(0,0,0) rot=(0.57735,0.57735,0.57735;2.0944rad)
  Support = -> [XZ_Plane072]
  sketch-geometry (23):
    g0: LineSegment [constr] StartX=-27.0262 StartY=-52 StartZ=0 EndX=32.4684 EndY=-52 EndZ=0
    g1: LineSegment [constr] StartX=-26.5915 StartY=-17 StartZ=0 EndX=27.3559 EndY=-17 EndZ=0
    g2: Circle [constr] CenterX=0 CenterY=0 CenterZ=0 NormalX=0 NormalY=0 NormalZ=1 AngleXU=0 Radius=1.75
    g3: LineSegment [constr] StartX=-7.5 StartY=2.28754 StartZ=0 EndX=-7.5 EndY=-69.1543 EndZ=0
    g4: LineSegment [constr] StartX=7.5 StartY=2.51533 StartZ=0 EndX=7.5 EndY=-69.1543 EndZ=0
    g5: LineSegment [constr] StartX=-14.793 StartY=-11 StartZ=0 EndX=13.8329 EndY=-11 EndZ=0
    g6: LineSegment [constr] StartX=0.017763 StartY=-22 StartZ=0 EndX=0.017763 EndY=-13 EndZ=0
    g7: LineSegment [constr] StartX=-12.2452 StartY=-35 StartZ=0 EndX=11.2356 EndY=-35 EndZ=0
    g8: LineSegment [constr] StartX=-4 StartY=-12.5552 StartZ=0 EndX=-4 EndY=-18.9221 EndZ=0
    g9: LineSegment [constr] StartX=4 StartY=-12.707 StartZ=0 EndX=4 EndY=-18.9221 EndZ=0
    g10: Circle CenterX=-4 CenterY=-17 CenterZ=0 NormalX=0 NormalY=0 NormalZ=1 AngleXU=0 Radius=2.1
    g11: Circle CenterX=4 CenterY=-17 CenterZ=0 NormalX=0 NormalY=0 NormalZ=1 AngleXU=0 Radius=2.1
    g12: ArcOfCircle CenterX=0 CenterY=0 CenterZ=0 NormalX=0 NormalY=0 NormalZ=1 AngleXU=0 Radius=13 StartAngle=4.15032 EndAngle=5.27446
    g13: LineSegment [constr] StartX=-26.6334 StartY=-65 StartZ=0 EndX=31.186 EndY=-65 EndZ=0
    g14: LineSegment StartX=-6.9282 StartY=-11 StartZ=0 EndX=-7.5 EndY=-11 EndZ=0
    g15: LineSegment StartX=-7.5 StartY=-11 StartZ=0 EndX=-7.5 EndY=-65 EndZ=0
    g16: LineSegment StartX=-7.5 StartY=-65 StartZ=0 EndX=7.5 EndY=-65 EndZ=0
    g17: LineSegment StartX=7.5 StartY=-65 StartZ=0 EndX=7.5 EndY=-11 EndZ=0
    g18: LineSegment StartX=7.5 StartY=-11 StartZ=0 EndX=6.9282 EndY=-11 EndZ=0
    g19: Circle CenterX=0 CenterY=-52 CenterZ=0 NormalX=0 NormalY=0 NormalZ=1 AngleXU=0 Radius=2.5
    g20: Circle CenterX=0 CenterY=-35 CenterZ=0 NormalX=0 NormalY=0 NormalZ=1 AngleXU=0 Radius=2.1
    g21: LineSegment [constr] StartX=-13.8843 StartY=-20 StartZ=0 EndX=11.4949 EndY=-20 EndZ=0
    g22: Circle CenterX=0.017763 CenterY=-20 CenterZ=0 NormalX=0 NormalY=0 NormalZ=1 AngleXU=0 Radius=1.1
  constraints (56):
    c: Horizontal(g0)
    c: DistanceY(g0,g-1) = 52
    c: Horizontal(g1)
    c: DistanceY(g1,g-1) = 17
    c: Coincident(g2,g-1)
    c: Radius(g2) = 1.75
    c: Vertical(g3)
    c: Vertical(g4)
    c: DistanceX(g3,g4) = 15
    c: Symmetric(g4,g3,g-2)
    c: Horizontal(g5)
    c: Vertical(g6)
    c: Horizontal(g7)
    c: Vertical(g8)
    c: Vertical(g9)
    c: Symmetric(g8,g9,g-2)
    c: DistanceX(g9,g4) = 3.5
    c: PointOnObject(g10,g8)
    c: PointOnObject(g11,g9)
    c: PointOnObject(g11,g1)
    c: PointOnObject(g10,g1)
    c: Radius(g10) = 2.1
    c: Radius(g11) = 2.1
    c: DistanceY(g5,g-1) = 11
    c: Coincident(g12,g-1)
    c: PointOnObject(g12,g5)
    c: PointOnObject(g12,g5)
    c: Radius(g12) = 13
    c: Horizontal(g13)
    c: Coincident(g14,g15)
    c: PointOnObject(g15,g13)
    c: Vertical(g15)
    c: Coincident(g15,g16)
    c: PointOnObject(g16,g13)
    c: Coincident(g16,g17)
    c: Vertical(g17)
    c: Coincident(g17,g18)
    c: Horizontal(g18)
    c: Coincident(g18,g12)
    c: Horizontal(g14)
    c: Coincident(g14,g12)
    c: PointOnObject(g16,g4)
    c: PointOnObject(g15,g3)
    c: DistanceY(g13,g5) = 54
    c: PointOnObject(g19,g-2)
    c: PointOnObject(g19,g0)
    c: Radius(g19) = 2.5
    c: DistanceY(g13,g7) = 30
    c: PointOnObject(g20,g-2)
    c: PointOnObject(g20,g7)
    c: Radius(g20) = 2.1
    c: Horizontal(g21)
    c: DistanceY(g21,g1) = 3
    c: PointOnObject(g22,g6)
    c: PointOnObject(g22,g21)
    c: Radius(g22) = 1.1
FEATURE [PartDesign::Pad] Pad029
  Length = 3
  Length2 = 100
  Placement = pos=(0,0,0) rot=(1,0,0;1.5708rad)
  Profile = -> Sketch039
  Type = 0
FEATURE [PartDesign::Body] Body051  label="blech_innen_R"
  Group = -> [Sketch039,Pad029]
  Origin = -> Origin071
  Placement = pos=(4.5,-17.1,-12) rot=(0,0,1;0rad)
  Tip = -> Pad029
FEATURE [Sketcher::SketchObject] Sketch040
  AttachmentOffset = pos=(0,0,0) rot=(0,1,0;1.5708rad)
  MapMode = 5
  Placement = pos=(0,0,0) rot=(0.57735,0.57735,0.57735;2.0944rad)
  Support = -> [XZ_Plane073]
  sketch-geometry (22):
    g0: LineSegment [constr] StartX=-27.0262 StartY=-52 StartZ=0 EndX=32.4684 EndY=-52 EndZ=0
    g1: LineSegment [constr] StartX=-26.5915 StartY=-17 StartZ=0 EndX=27.3559 EndY=-17 EndZ=0
    g2: Circle [constr] CenterX=0 CenterY=0 CenterZ=0 NormalX=0 NormalY=0 NormalZ=1 AngleXU=0 Radius=1.75
    g3: ArcOfCircle CenterX=0 CenterY=0 CenterZ=0 NormalX=0 NormalY=0 NormalZ=1 AngleXU=0 Radius=13 StartAngle=4.15032 EndAngle=5.27446
    g4: LineSegment [constr] StartX=-7.5 StartY=2.28754 StartZ=0 EndX=-7.5 EndY=-39.0262 EndZ=0
    g5: LineSegment [constr] StartX=7.5 StartY=2.51533 StartZ=0 EndX=7.5 EndY=-39.0262 EndZ=0
    g6: LineSegment [constr] StartX=-14.4286 StartY=-11 StartZ=0 EndX=14.1973 EndY=-11 EndZ=0
    g7: LineSegment [constr] StartX=-2.4e-15 StartY=-22 StartZ=0 EndX=-2.4e-15 EndY=-13 EndZ=0
    g8: LineSegment [constr] StartX=-12.3986 StartY=-42 StartZ=0 EndX=11.5955 EndY=-42 EndZ=0
    g9: LineSegment [constr] StartX=-4 StartY=-12.5552 StartZ=0 EndX=-4 EndY=-18.9221 EndZ=0
    g10: LineSegment [constr] StartX=4 StartY=-12.707 StartZ=0 EndX=4 EndY=-18.9221 EndZ=0
    g11: Circle CenterX=-4 CenterY=-17 CenterZ=0 NormalX=0 NormalY=0 NormalZ=1 AngleXU=0 Radius=2.2
    g12: Circle CenterX=4 CenterY=-17 CenterZ=0 NormalX=0 NormalY=0 NormalZ=1 AngleXU=0 Radius=2.2
    g13: LineSegment StartX=-6.9282 StartY=-11 StartZ=0 EndX=-7.5 EndY=-11 EndZ=0
    g14: LineSegment StartX=-7.5 StartY=-11 StartZ=0 EndX=-7.5 EndY=-42 EndZ=0
    g15: LineSegment StartX=6.9282 StartY=-11 StartZ=0 EndX=7.5 EndY=-11 EndZ=0
    g16: LineSegment StartX=7.5 StartY=-11 StartZ=0 EndX=7.5 EndY=-42 EndZ=0
    g17: LineSegment StartX=7.5 StartY=-42 StartZ=0 EndX=-7.5 EndY=-42 EndZ=0
    g18: LineSegment [constr] StartX=-23.1205 StartY=-35 StartZ=0 EndX=25.2757 EndY=-35 EndZ=0
    g19: Circle CenterX=0 CenterY=-35 CenterZ=0 NormalX=0 NormalY=0 NormalZ=1 AngleXU=0 Radius=2.2
    g20: LineSegment [constr] StartX=-11.0622 StartY=-20 StartZ=0 EndX=11.4815 EndY=-20 EndZ=0
    g21: Circle CenterX=-2.4e-15 CenterY=-20 CenterZ=0 NormalX=0 NormalY=0 NormalZ=1 AngleXU=0 Radius=1.1
  constraints (53):
    c: Horizontal(g0)
    c: DistanceY(g0,g-1) = 52
    c: Horizontal(g1)
    c: DistanceY(g1,g-1) = 17
    c: Coincident(g2,g-1)
    c: Radius(g2) = 1.75
    c: Coincident(g3,g-1)
    c: Vertical(g4)
    c: Vertical(g5)
    c: DistanceX(g4,g5) = 15
    c: Symmetric(g5,g4,g-2)
    c: Horizontal(g6)
    c: Radius(g3) = 13
    c: PointOnObject(g3,g6)
    c: PointOnObject(g3,g6)
    c: Vertical(g7)
    c: Perpendicular(g7,g3) = 4.71239
    c: Horizontal(g8)
    c: PointOnObject(g17,g8)
    c: Vertical(g9)
    c: Vertical(g10)
    c: Symmetric(g9,g10,g-2)
    c: PointOnObject(g11,g9)
    c: PointOnObject(g12,g10)
    c: PointOnObject(g12,g1)
    c: PointOnObject(g11,g1)
    c: Radius(g11) = 2.2
    c: Radius(g12) = 2.2
    c: Horizontal(g13)
    c: Coincident(g13,g14)
    c: Vertical(g14)
    c: Coincident(g15,g16)
    c: Vertical(g16)
    c: Coincident(g16,g17)
    c: Horizontal(g15)
    c: Horizontal(g17)
    c: Coincident(g13,g3)
    c: Coincident(g15,g3)
    c: PointOnObject(g14,g4)
    c: PointOnObject(g16,g5)
    c: DistanceY(g6,g3) = 11
    c: Coincident(g17,g14)
    c: DistanceY(g8,g6) = 31
    c: Horizontal(g18)
    c: DistanceY(g18,g1) = 18
    c: PointOnObject(g19,g-2)
    c: PointOnObject(g19,g18)
    c: Radius(g19) = 2.2
    c: Horizontal(g20)
    c: DistanceY(g20,g1) = 3
    c: PointOnObject(g21,g7)
    c: PointOnObject(g21,g20)
    c: Radius(g21) = 1.1
FEATURE [PartDesign::Pad] Pad030
  Length = 2.75
  Length2 = 100
  Placement = pos=(0,0,0) rot=(1,0,0;1.5708rad)
  Profile = -> Sketch040
  Type = 0
FEATURE [PartDesign::Body] Body052  label="distance_aussen_L"
  Group = -> [Sketch040,Pad030]
  Origin = -> Origin072
  Placement = pos=(7.5,-17.1,-12) rot=(0,0,1;0rad)
  Tip = -> Pad030
FEATURE [App::DocumentObjectGroup] Gruppe012  label="innen"
  Group = -> [Body045]
FEATURE [Sketcher::SketchObject] Sketch041
  AttachmentOffset = pos=(0,0,0) rot=(0,1,0;1.5708rad)
  MapMode = 5
  Placement = pos=(0,0,0) rot=(0.57735,0.57735,0.57735;2.0944rad)
  Support = -> [XZ_Plane074]
  sketch-geometry (22):
    g0: LineSegment [constr] StartX=-27.0262 StartY=-52 StartZ=0 EndX=32.4684 EndY=-52 EndZ=0
    g1: LineSegment [constr] StartX=-26.5915 StartY=-17 StartZ=0 EndX=27.3559 EndY=-17 EndZ=0
    g2: Circle [constr] CenterX=0 CenterY=0 CenterZ=0 NormalX=0 NormalY=0 NormalZ=1 AngleXU=0 Radius=1.75
    g3: ArcOfCircle CenterX=0 CenterY=0 CenterZ=0 NormalX=0 NormalY=0 NormalZ=1 AngleXU=0 Radius=13 StartAngle=4.15032 EndAngle=5.27446
    g4: LineSegment [constr] StartX=-7.5 StartY=2.28754 StartZ=0 EndX=-7.5 EndY=-39.0262 EndZ=0
    g5: LineSegment [constr] StartX=7.5 StartY=2.51533 StartZ=0 EndX=7.5 EndY=-39.0262 EndZ=0
    g6: LineSegment [constr] StartX=-14.4286 StartY=-11 StartZ=0 EndX=14.1973 EndY=-11 EndZ=0
    g7: LineSegment [constr] StartX=-2.4e-15 StartY=-22 StartZ=0 EndX=-2.4e-15 EndY=-13 EndZ=0
    g8: LineSegment [constr] StartX=-12.3986 StartY=-42 StartZ=0 EndX=11.5955 EndY=-42 EndZ=0
    g9: LineSegment [constr] StartX=-4 StartY=-12.5552 StartZ=0 EndX=-4 EndY=-18.9221 EndZ=0
    g10: LineSegment [constr] StartX=4 StartY=-12.707 StartZ=0 EndX=4 EndY=-18.9221 EndZ=0
    g11: Circle CenterX=-4 CenterY=-17 CenterZ=0 NormalX=0 NormalY=0 NormalZ=1 AngleXU=0 Radius=2.2
    g12: Circle CenterX=4 CenterY=-17 CenterZ=0 NormalX=0 NormalY=0 NormalZ=1 AngleXU=0 Radius=2.2
    g13: LineSegment StartX=-6.9282 StartY=-11 StartZ=0 EndX=-7.5 EndY=-11 EndZ=0
    g14: LineSegment StartX=-7.5 StartY=-11 StartZ=0 EndX=-7.5 EndY=-42 EndZ=0
    g15: LineSegment StartX=6.9282 StartY=-11 StartZ=0 EndX=7.5 EndY=-11 EndZ=0
    g16: LineSegment StartX=7.5 StartY=-11 StartZ=0 EndX=7.5 EndY=-42 EndZ=0
    g17: LineSegment StartX=7.5 StartY=-42 StartZ=0 EndX=-7.5 EndY=-42 EndZ=0
    g18: LineSegment [constr] StartX=-23.1205 StartY=-35 StartZ=0 EndX=25.2757 EndY=-35 EndZ=0
    g19: Circle CenterX=0 CenterY=-35 CenterZ=0 NormalX=0 NormalY=0 NormalZ=1 AngleXU=0 Radius=2.2
    g20: LineSegment [constr] StartX=-8.67569 StartY=-20 StartZ=0 EndX=10.563 EndY=-20 EndZ=0
    g21: Circle CenterX=-2.4e-15 CenterY=-20 CenterZ=0 NormalX=0 NormalY=0 NormalZ=1 AngleXU=0 Radius=1.1
  constraints (53):
    c: Horizontal(g0)
    c: DistanceY(g0,g-1) = 52
    c: Horizontal(g1)
    c: DistanceY(g1,g-1) = 17
    c: Coincident(g2,g-1)
    c: Radius(g2) = 1.75
    c: Coincident(g3,g-1)
    c: Vertical(g4)
    c: Vertical(g5)
    c: DistanceX(g4,g5) = 15
    c: Symmetric(g5,g4,g-2)
    c: Horizontal(g6)
    c: Radius(g3) = 13
    c: PointOnObject(g3,g6)
    c: PointOnObject(g3,g6)
    c: Vertical(g7)
    c: Perpendicular(g7,g3) = 4.71239
    c: Horizontal(g8)
    c: PointOnObject(g17,g8)
    c: Vertical(g9)
    c: Vertical(g10)
    c: Symmetric(g9,g10,g-2)
    c: PointOnObject(g11,g9)
    c: PointOnObject(g12,g10)
    c: PointOnObject(g12,g1)
    c: PointOnObject(g11,g1)
    c: Radius(g11) = 2.2
    c: Radius(g12) = 2.2
    c: Horizontal(g13)
    c: Coincident(g13,g14)
    c: Vertical(g14)
    c: Coincident(g15,g16)
    c: Vertical(g16)
    c: Coincident(g16,g17)
    c: Horizontal(g15)
    c: Horizontal(g17)
    c: Coincident(g13,g3)
    c: Coincident(g15,g3)
    c: PointOnObject(g14,g4)
    c: PointOnObject(g16,g5)
    c: DistanceY(g6,g3) = 11
    c: Coincident(g17,g14)
    c: DistanceY(g8,g6) = 31
    c: Horizontal(g18)
    c: DistanceY(g18,g1) = 18
    c: PointOnObject(g19,g-2)
    c: PointOnObject(g19,g18)
    c: Radius(g19) = 2.2
    c: Horizontal(g20)
    c: DistanceY(g20,g1) = 3
    c: PointOnObject(g21,g7)
    c: PointOnObject(g21,g20)
    c: Radius(g21) = 1.1
FEATURE [PartDesign::Pad] Pad031
  Length = 2.75
  Length2 = 100
  Placement = pos=(0,0,0) rot=(1,0,0;1.5708rad)
  Profile = -> Sketch041
  Type = 0
FEATURE [PartDesign::Body] Body053  label="distance_aussen_R"
  Group = -> [Sketch041,Pad031]
  Origin = -> Origin073
  Placement = pos=(-10.25,-17.1,-12) rot=(0,0,1;0rad)
  Tip = -> Pad031
FEATURE [App::DocumentObjectGroup] Gruppe013  label="aussen"
  Group = -> [Body052,Body053]
FEATURE [App::DocumentObjectGroup] Group021  label="swinge-distance"
  Group = -> [Body044,Gruppe012,Gruppe013]
FEATURE [App::DocumentObjectGroup] Gruppe014  label="innen001"
  Group = -> [Body051,Body047]
FEATURE [Sketcher::SketchObject] Sketch042
  AttachmentOffset = pos=(0,0,0) rot=(0,1,0;1.5708rad)
  MapMode = 5
  Placement = pos=(0,0,0) rot=(0.57735,0.57735,0.57735;2.0944rad)
  Support = -> [XZ_Plane075]
  sketch-geometry (21):
    g0: LineSegment [constr] StartX=-27.0262 StartY=-52 StartZ=0 EndX=32.4684 EndY=-52 EndZ=0
    g1: LineSegment [constr] StartX=-26.5915 StartY=-17 StartZ=0 EndX=27.3559 EndY=-17 EndZ=0
    g2: Circle CenterX=0 CenterY=0 CenterZ=0 NormalX=0 NormalY=0 NormalZ=1 AngleXU=0 Radius=1.75
    g3: LineSegment [constr] StartX=-7.5 StartY=16.3062 StartZ=0 EndX=-7.5 EndY=-69.1543 EndZ=0
    g4: LineSegment [constr] StartX=7.5 StartY=16.4605 StartZ=0 EndX=7.5 EndY=-69.1543 EndZ=0
    g5: LineSegment [constr] StartX=-16.1413 StartY=7.5 StartZ=0 EndX=0 EndY=7.5 EndZ=0
    g6: LineSegment [constr] StartX=0.035815 StartY=-22 StartZ=0 EndX=0.035815 EndY=-13 EndZ=0
    g7: LineSegment [constr] StartX=-12.2452 StartY=-22.7126 StartZ=0 EndX=11.7489 EndY=-22.7126 EndZ=0
    g8: LineSegment [constr] StartX=-4 StartY=-12.5552 StartZ=0 EndX=-4 EndY=-18.9221 EndZ=0
    g9: LineSegment [constr] StartX=4 StartY=-12.707 StartZ=0 EndX=4 EndY=-18.9221 EndZ=0
    g10: Circle CenterX=-4 CenterY=-17 CenterZ=0 NormalX=0 NormalY=0 NormalZ=1 AngleXU=0 Radius=2.1
    g11: Circle CenterX=4 CenterY=-17 CenterZ=0 NormalX=0 NormalY=0 NormalZ=1 AngleXU=0 Radius=2.1
    g12: LineSegment [constr] StartX=-26.6334 StartY=-42 StartZ=0 EndX=31.186 EndY=-42 EndZ=0
    g13: LineSegment StartX=-7.5 StartY=1.81973e-06 StartZ=0 EndX=-7.5 EndY=-42 EndZ=0
    g14: LineSegment StartX=-7.5 StartY=-42 StartZ=0 EndX=7.5 EndY=-42 EndZ=0
    g15: LineSegment StartX=7.5 StartY=-42 StartZ=0 EndX=7.5 EndY=1.82381e-06 EndZ=0
    g16: ArcOfCircle CenterX=0 CenterY=0 CenterZ=0 NormalX=0 NormalY=0 NormalZ=1 AngleXU=0 Radius=7.5 StartAngle=2.43174e-07 EndAngle=3.14159
    g17: LineSegment [constr] StartX=-17.6149 StartY=-35 StartZ=0 EndX=11.6816 EndY=-35 EndZ=0
    g18: Circle CenterX=0 CenterY=-35 CenterZ=0 NormalX=0 NormalY=0 NormalZ=1 AngleXU=0 Radius=2.1
    g19: LineSegment [constr] StartX=-16.676 StartY=-20 StartZ=0 EndX=17.111 EndY=-20 EndZ=0
    g20: Circle CenterX=0.035815 CenterY=-20 CenterZ=0 NormalX=0 NormalY=0 NormalZ=1 AngleXU=0 Radius=1.1
  constraints (48):
    c: Horizontal(g0)
    c: DistanceY(g0,g-1) = 52
    c: Horizontal(g1)
    c: DistanceY(g1,g-1) = 17
    c: Coincident(g2,g-1)
    c: Radius(g2) = 1.75
    c: Vertical(g3)
    c: Vertical(g4)
    c: DistanceX(g3,g4) = 15
    c: Symmetric(g4,g3,g-2)
    c: Horizontal(g5)
    c: Vertical(g6)
    c: Horizontal(g7)
    c: Vertical(g8)
    c: Vertical(g9)
    c: Symmetric(g8,g9,g-2)
    c: DistanceX(g9,g4) = 3.5
    c: PointOnObject(g10,g8)
    c: PointOnObject(g11,g9)
    c: PointOnObject(g11,g1)
    c: PointOnObject(g10,g1)
    c: Radius(g10) = 2.1
    c: Radius(g11) = 2.1
    c: Horizontal(g12)
    c: PointOnObject(g13,g12)
    c: Vertical(g13)
    c: Coincident(g13,g14)
    c: PointOnObject(g14,g12)
    c: Coincident(g14,g15)
    c: Vertical(g15)
    c: PointOnObject(g14,g4)
    c: PointOnObject(g13,g3)
    c: Coincident(g16,g-1)
    c: Radius(g16) = 7.5
    c: Coincident(g13,g16)
    c: Coincident(g15,g16)
    c: Horizontal(g17)
    c: DistanceY(g12,g17) = 7
    c: PointOnObject(g18,g-2)
    c: PointOnObject(g18,g17)
    c: Radius(g18) = 2.1
    c: Tangent(g5,g16) = 1.5708
    c: DistanceY(g12,g5) = 49.5
    c: Horizontal(g19)
    c: DistanceY(g19,g1) = 3
    c: PointOnObject(g20,g6)
    c: PointOnObject(g20,g19)
    c: Radius(g20) = 1.1
FEATURE [PartDesign::Pad] Pad032
  Length = 3
  Length2 = 100
  Placement = pos=(0,0,0) rot=(1,0,0;1.5708rad)
  Profile = -> Sketch042
  Type = 0
FEATURE [PartDesign::Body] Body054  label="blech_aussen_R"
  Group = -> [Sketch042,Pad032]
  Origin = -> Origin074
  Placement = pos=(10.25,-17.1,-12) rot=(0,0,1;0rad)
  Tip = -> Pad032
FEATURE [Sketcher::SketchObject] Sketch043
  AttachmentOffset = pos=(0,0,0) rot=(0,1,0;1.5708rad)
  MapMode = 5
  Placement = pos=(0,0,0) rot=(0.57735,0.57735,0.57735;2.0944rad)
  Support = -> [XZ_Plane076]
  sketch-geometry (21):
    g0: LineSegment [constr] StartX=-27.0262 StartY=-52 StartZ=0 EndX=32.4684 EndY=-52 EndZ=0
    g1: LineSegment [constr] StartX=-26.5915 StartY=-17 StartZ=0 EndX=27.3559 EndY=-17 EndZ=0
    g2: Circle CenterX=0 CenterY=0 CenterZ=0 NormalX=0 NormalY=0 NormalZ=1 AngleXU=0 Radius=1.75
    g3: LineSegment [constr] StartX=-7.5 StartY=16.3062 StartZ=0 EndX=-7.5 EndY=-69.1543 EndZ=0
    g4: LineSegment [constr] StartX=7.5 StartY=16.4605 StartZ=0 EndX=7.5 EndY=-69.1543 EndZ=0
    g5: LineSegment [constr] StartX=-21.859 StartY=7.5 StartZ=0 EndX=0 EndY=7.5 EndZ=0
    g6: LineSegment [constr] StartX=0.0707107 StartY=-22 StartZ=0 EndX=0.0707107 EndY=-13 EndZ=0
    g7: LineSegment [constr] StartX=-12.2452 StartY=-22.7126 StartZ=0 EndX=11.7489 EndY=-22.7126 EndZ=0
    g8: LineSegment [constr] StartX=-4 StartY=-12.5552 StartZ=0 EndX=-4 EndY=-18.9221 EndZ=0
    g9: LineSegment [constr] StartX=4 StartY=-12.707 StartZ=0 EndX=4 EndY=-18.9221 EndZ=0
    g10: Circle CenterX=-4 CenterY=-17 CenterZ=0 NormalX=0 NormalY=0 NormalZ=1 AngleXU=0 Radius=2.1
    g11: Circle CenterX=4 CenterY=-17 CenterZ=0 NormalX=0 NormalY=0 NormalZ=1 AngleXU=0 Radius=2.1
    g12: LineSegment [constr] StartX=-26.6334 StartY=-42 StartZ=0 EndX=31.186 EndY=-42 EndZ=0
    g13: LineSegment StartX=-7.5 StartY=-1.57637e-07 StartZ=0 EndX=-7.5 EndY=-42 EndZ=0
    g14: LineSegment StartX=-7.5 StartY=-42 StartZ=0 EndX=7.5 EndY=-42 EndZ=0
    g15: LineSegment StartX=7.5 StartY=-42 StartZ=0 EndX=7.5 EndY=-1.75426e-07 EndZ=0
    g16: ArcOfCircle CenterX=0 CenterY=0 CenterZ=0 NormalX=0 NormalY=0 NormalZ=1 AngleXU=0 Radius=7.5 StartAngle=6.28319 EndAngle=9.42478
    g17: LineSegment [constr] StartX=-17.6149 StartY=-35 StartZ=0 EndX=11.6816 EndY=-35 EndZ=0
    g18: Circle CenterX=0 CenterY=-35 CenterZ=0 NormalX=0 NormalY=0 NormalZ=1 AngleXU=0 Radius=2.1
    g19: LineSegment [constr] StartX=-10.4805 StartY=-20 StartZ=0 EndX=10.8456 EndY=-20 EndZ=0
    g20: Circle CenterX=0.0707107 CenterY=-20 CenterZ=0 NormalX=0 NormalY=0 NormalZ=1 AngleXU=0 Radius=1.1
  constraints (48):
    c: Horizontal(g0)
    c: DistanceY(g0,g-1) = 52
    c: Horizontal(g1)
    c: DistanceY(g1,g-1) = 17
    c: Coincident(g2,g-1)
    c: Radius(g2) = 1.75
    c: Vertical(g3)
    c: Vertical(g4)
    c: DistanceX(g3,g4) = 15
    c: Symmetric(g4,g3,g-2)
    c: Horizontal(g5)
    c: Vertical(g6)
    c: Horizontal(g7)
    c: Vertical(g8)
    c: Vertical(g9)
    c: Symmetric(g8,g9,g-2)
    c: DistanceX(g9,g4) = 3.5
    c: PointOnObject(g10,g8)
    c: PointOnObject(g11,g9)
    c: PointOnObject(g11,g1)
    c: PointOnObject(g10,g1)
    c: Radius(g10) = 2.1
    c: Radius(g11) = 2.1
    c: Horizontal(g12)
    c: PointOnObject(g13,g12)
    c: Vertical(g13)
    c: Coincident(g13,g14)
    c: PointOnObject(g14,g12)
    c: Coincident(g14,g15)
    c: Vertical(g15)
    c: PointOnObject(g14,g4)
    c: PointOnObject(g13,g3)
    c: Coincident(g16,g-1)
    c: Radius(g16) = 7.5
    c: Coincident(g13,g16)
    c: Coincident(g15,g16)
    c: Horizontal(g17)
    c: DistanceY(g12,g17) = 7
    c: PointOnObject(g18,g-2)
    c: PointOnObject(g18,g17)
    c: Radius(g18) = 2.1
    c: Tangent(g5,g16) = 1.5708
    c: DistanceY(g12,g5) = 49.5
    c: Horizontal(g19)
    c: DistanceY(g19,g1) = 3
    c: PointOnObject(g20,g6)
    c: PointOnObject(g20,g19)
    c: Radius(g20) = 1.1
FEATURE [PartDesign::Pad] Pad033
  Length = 3
  Length2 = 100
  Placement = pos=(0,0,0) rot=(1,0,0;1.5708rad)
  Profile = -> Sketch043
  Type = 0
FEATURE [PartDesign::Body] Body055  label="blech_aussen_L"
  Group = -> [Sketch043,Pad033]
  Origin = -> Origin075
  Placement = pos=(-13.25,-17.1,-12) rot=(0,0,1;0rad)
  Tip = -> Pad033
FEATURE [App::DocumentObjectGroup] Gruppe015  label="aussen001"
  Group = -> [Body054,Body055]
FEATURE [App::DocumentObjectGroup] Group020  label="schwinge-bleche"
  Group = -> [Body040,Body046,Gruppe014,Gruppe015]
FEATURE [App::Part] Part016  label="schwinge"
  Group = -> [Group018,Body039,Group020,Body040,Group021,Body041,Group022,Body043,Body044,Body045,Body046,Body047,Gruppe011,Body049,Body050,Body051,Body052,Gruppe012,Gruppe013,Body053,Gruppe014,Gruppe015,Body054,Body055]
  Origin = -> Origin053
  Placement = pos=(36.4481,-22.1668,16.5) rot=(0,0,1;6.10865rad)
FEATURE [Mesh::Feature] Mesh  label="~KsM_117"
FEATURE [Mesh::Feature] Mesh001  label="~KsRL_117"
FEATURE [Mesh::Feature] Mesh002  label="~KsM_118"
FEATURE [App::DocumentObjectGroup] Gruppe016  label="schwinge001"
  Group = -> [Mesh,Mesh001,Mesh002]
FEATURE [App::DocumentObjectGroup] Group  label="mesh"
  Group = -> [Group001,Gruppe,Group006,Gruppe008,Gruppe010,Gruppe016]
